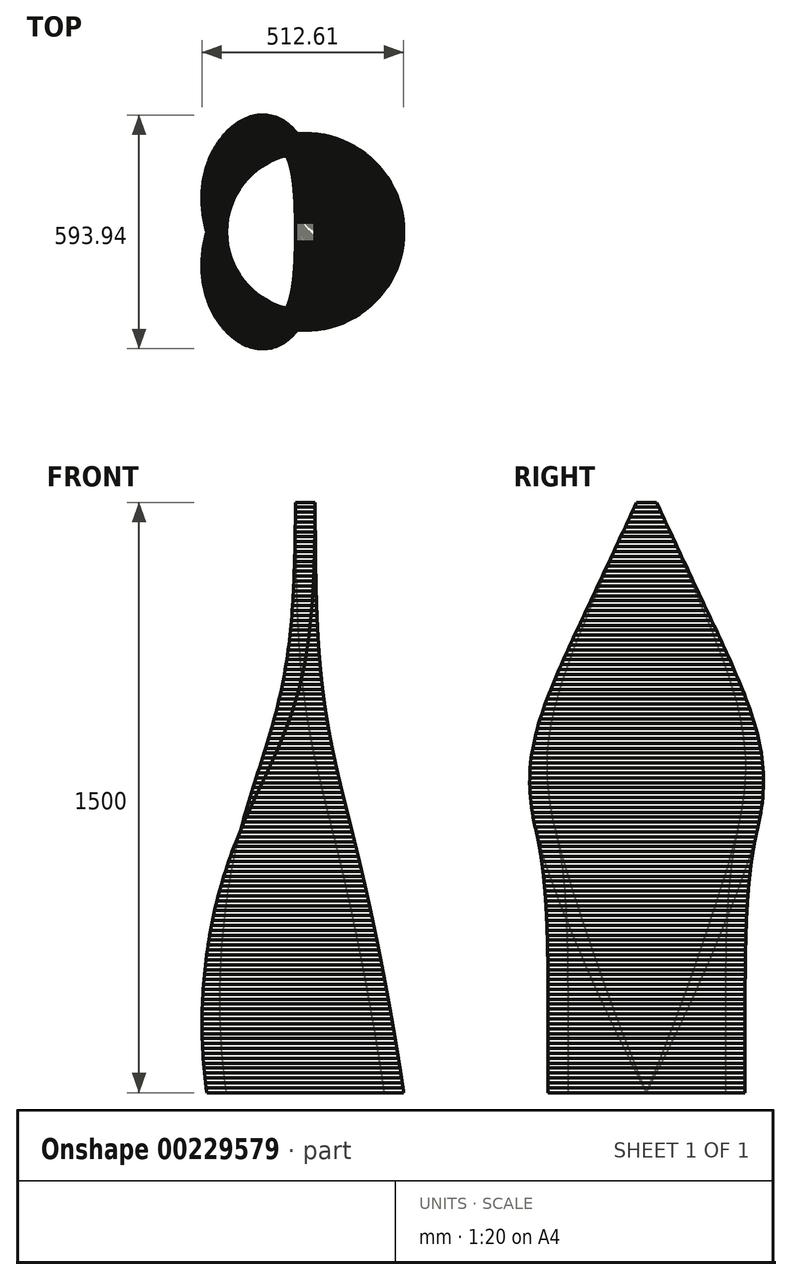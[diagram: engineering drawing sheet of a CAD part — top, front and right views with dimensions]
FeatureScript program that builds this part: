
annotation { "Feature Type Name" : "Feature", "Feature Type Description" : "" }
export const myFeature = defineFeature(function(context is Context, id is Id, definition is map)
    precondition{}
    {
        {
            var Q0;
            Q0=qCreatedBy(makeId("Top.planeOp"),FACE);
            var sketch = newSketch(context, id + "F0", { "sketchPlane" : qUnion([Q0])});
            skLineSegment(sketch, "E0", {"start": v(-200.02, 0.04) * mm, "end": v(-250.02, 0.06) * mm});
            skLineSegment(sketch, "E1", {"start": v(-200.02, -0.04) * mm, "end": v(-250.02, -0.06) * mm});
            skArc(sketch, "E2", {"start": v(-200.02, -0.04) * mm, "mid": v(199.98, 0) * mm, "end": v(-200.02, 0.04) * mm});
            skArc(sketch, "E3", {"start": v(-250.02, -0.06) * mm, "mid": v(249.98, 0) * mm, "end": v(-250.02, 0.06) * mm});
            skSolve(sketch);
        }
        {
            var Q0;
            Q0=qCreatedBy(makeId("Top.planeOp"),FACE);
            cPlane(context, id + "F1", {"entities" : qUnion([Q0]), "cplaneType" : CPlaneType.OFFSET, "offset" : 12.5 * mm, "width" : 150 * mm, "height" : 150 * mm});
        }
        {
            var Q0;
            Q0=qCreatedBy(id+"F1.planeOp",FACE);
            var sketch = newSketch(context, id + "F2", { "sketchPlane" : qUnion([Q0])});
            skLineSegment(sketch, "E4", {"start": v(-201.78, 5.1) * mm, "end": v(-251.77, 6.37) * mm});
            skLineSegment(sketch, "E5", {"start": v(-201.78, -5.1) * mm, "end": v(-251.77, -6.37) * mm});
            skArc(sketch, "E6", {"start": v(-201.78, -5.1) * mm, "mid": v(198.15, 0) * mm, "end": v(-201.78, 5.1) * mm});
            skArc(sketch, "E7", {"start": v(-251.77, -6.37) * mm, "mid": v(248.15, 0) * mm, "end": v(-251.77, 6.37) * mm});
            skSolve(sketch);
        }
        {
            var Q0;
            Q0 = qSketchRegion(id + "F0", true);
            var Q1;
            Q1 = qSketchRegion(id + "F2", true);
            loft(context, id + "F3", {"sheetProfilesArray" : [{ "sheetProfileEntities" : qUnion([Q0]) }, { "sheetProfileEntities" : qUnion([Q1]) }]});
        }
        {
            var Q0;
            Q0=qCreatedBy(makeId("Top.planeOp"),FACE);
            cPlane(context, id + "F4", {"entities" : qUnion([Q0]), "cplaneType" : CPlaneType.OFFSET, "offset" : 25 * mm, "width" : 150 * mm, "height" : 150 * mm});
        }
        {
            var Q0;
            Q0=qCreatedBy(id+"F4.planeOp",FACE);
            var sketch = newSketch(context, id + "F5", { "sketchPlane" : qUnion([Q0])});
            skLineSegment(sketch, "E8", {"start": v(-203.45, 10.14) * mm, "end": v(-253.38, 12.68) * mm});
            skLineSegment(sketch, "E9", {"start": v(-203.45, -10.14) * mm, "end": v(-253.38, -12.68) * mm});
            skArc(sketch, "E10", {"start": v(-203.45, -10.14) * mm, "mid": v(196.3, 0) * mm, "end": v(-203.45, 10.14) * mm});
            skArc(sketch, "E11", {"start": v(-253.38, -12.68) * mm, "mid": v(246.3, 0) * mm, "end": v(-253.38, 12.68) * mm});
            skSolve(sketch);
        }
        {
            var Q1;
            Q1 = qSketchRegion(id + "F2", true);
            var Q2;
            Q2 = qSketchRegion(id + "F5", true);
            loft(context, id + "F6", {"sheetProfilesArray" : [{ "sheetProfileEntities" : qUnion([Q1]) }, { "sheetProfileEntities" : qUnion([Q2]) }]});
        }
        {
            var Q0;
            Q0=qCreatedBy(id+"F1.planeOp",FACE);
            cPlane(context, id + "F7", {"entities" : qUnion([Q0]), "cplaneType" : CPlaneType.OFFSET, "offset" : 25 * mm, "width" : 150 * mm, "height" : 150 * mm});
        }
        {
            var Q0;
            Q0=qCreatedBy(id+"F7.planeOp",FACE);
            var sketch = newSketch(context, id + "F8", { "sketchPlane" : qUnion([Q0])});
            skLineSegment(sketch, "E12", {"start": v(-205.02, 15.18) * mm, "end": v(-254.87, 18.98) * mm});
            skLineSegment(sketch, "E13", {"start": v(-205.02, -15.18) * mm, "end": v(-254.87, -18.98) * mm});
            skArc(sketch, "E14", {"start": v(-205.02, -15.18) * mm, "mid": v(194.4, 0) * mm, "end": v(-205.02, 15.18) * mm});
            skArc(sketch, "E15", {"start": v(-254.87, -18.98) * mm, "mid": v(244.4, 0) * mm, "end": v(-254.87, 18.98) * mm});
            skSolve(sketch);
        }
        {
            var Q1;
            Q1 = qSketchRegion(id + "F5", true);
            var Q2;
            Q2 = qSketchRegion(id + "F8", true);
            loft(context, id + "F9", {"sheetProfilesArray" : [{ "sheetProfileEntities" : qUnion([Q1]) }, { "sheetProfileEntities" : qUnion([Q2]) }]});
        }
        {
            var Q0;
            Q0=qCreatedBy(id+"F4.planeOp",FACE);
            cPlane(context, id + "F10", {"entities" : qUnion([Q0]), "cplaneType" : CPlaneType.OFFSET, "offset" : 25 * mm, "width" : 150 * mm, "height" : 150 * mm});
        }
        {
            var Q0;
            Q0=qCreatedBy(id+"F10.planeOp",FACE);
            var sketch = newSketch(context, id + "F11", { "sketchPlane" : qUnion([Q0])});
            skLineSegment(sketch, "E16", {"start": v(-206.49, 20.21) * mm, "end": v(-256.23, 25.26) * mm});
            skLineSegment(sketch, "E17", {"start": v(-206.49, -20.21) * mm, "end": v(-256.23, -25.26) * mm});
            skArc(sketch, "E18", {"start": v(-206.49, -20.21) * mm, "mid": v(192.5, 0) * mm, "end": v(-206.49, 20.21) * mm});
            skArc(sketch, "E19", {"start": v(-256.23, -25.26) * mm, "mid": v(242.5, 0) * mm, "end": v(-256.23, 25.26) * mm});
            skSolve(sketch);
        }
        {
            var Q1;
            Q1 = qSketchRegion(id + "F8", true);
            var Q2;
            Q2 = qSketchRegion(id + "F11", true);
            loft(context, id + "F12", {"sheetProfilesArray" : [{ "sheetProfileEntities" : qUnion([Q1]) }, { "sheetProfileEntities" : qUnion([Q2]) }]});
        }
        {
            var Q0;
            Q0=qCreatedBy(id+"F7.planeOp",FACE);
            cPlane(context, id + "F13", {"entities" : qUnion([Q0]), "cplaneType" : CPlaneType.OFFSET, "offset" : 25 * mm, "width" : 150 * mm, "height" : 150 * mm});
        }
        {
            var Q0;
            Q0=qCreatedBy(id+"F13.planeOp",FACE);
            var sketch = newSketch(context, id + "F14", { "sketchPlane" : qUnion([Q0])});
            skLineSegment(sketch, "E20", {"start": v(-207.86, 25.23) * mm, "end": v(-257.46, 31.54) * mm});
            skLineSegment(sketch, "E21", {"start": v(-207.86, -25.23) * mm, "end": v(-257.46, -31.54) * mm});
            skArc(sketch, "E22", {"start": v(-207.86, -25.23) * mm, "mid": v(190.55, 0) * mm, "end": v(-207.86, 25.23) * mm});
            skArc(sketch, "E23", {"start": v(-257.46, -31.54) * mm, "mid": v(240.55, 0) * mm, "end": v(-257.46, 31.54) * mm});
            skSolve(sketch);
        }
        {
            var Q1;
            Q1 = qSketchRegion(id + "F11", true);
            var Q2;
            Q2 = qSketchRegion(id + "F14", true);
            loft(context, id + "F15", {"sheetProfilesArray" : [{ "sheetProfileEntities" : qUnion([Q1]) }, { "sheetProfileEntities" : qUnion([Q2]) }]});
        }
        {
            var Q0;
            Q0=qCreatedBy(id+"F10.planeOp",FACE);
            cPlane(context, id + "F16", {"entities" : qUnion([Q0]), "cplaneType" : CPlaneType.OFFSET, "offset" : 25 * mm, "width" : 150 * mm, "height" : 150 * mm});
        }
        {
            var Q0;
            Q0=qCreatedBy(id+"F16.planeOp",FACE);
            var sketch = newSketch(context, id + "F17", { "sketchPlane" : qUnion([Q0])});
            skLineSegment(sketch, "E24", {"start": v(-209.12, 30.23) * mm, "end": v(-258.55, 37.8) * mm});
            skLineSegment(sketch, "E25", {"start": v(-209.12, -30.23) * mm, "end": v(-258.55, -37.8) * mm});
            skArc(sketch, "E26", {"start": v(-209.12, -30.23) * mm, "mid": v(188.58, 0) * mm, "end": v(-209.12, 30.23) * mm});
            skArc(sketch, "E27", {"start": v(-258.55, -37.8) * mm, "mid": v(238.58, 0) * mm, "end": v(-258.55, 37.8) * mm});
            skSolve(sketch);
        }
        {
            var Q1;
            Q1 = qSketchRegion(id + "F14", true);
            var Q2;
            Q2 = qSketchRegion(id + "F17", true);
            loft(context, id + "F18", {"sheetProfilesArray" : [{ "sheetProfileEntities" : qUnion([Q1]) }, { "sheetProfileEntities" : qUnion([Q2]) }]});
        }
        {
            var Q0;
            Q0=qCreatedBy(id+"F13.planeOp",FACE);
            cPlane(context, id + "F19", {"entities" : qUnion([Q0]), "cplaneType" : CPlaneType.OFFSET, "offset" : 25 * mm, "width" : 150 * mm, "height" : 150 * mm});
        }
        {
            var Q0;
            Q0=qCreatedBy(id+"F19.planeOp",FACE);
            var sketch = newSketch(context, id + "F20", { "sketchPlane" : qUnion([Q0])});
            skLineSegment(sketch, "E28", {"start": v(-210.3, 35.22) * mm, "end": v(-259.51, 44.02) * mm});
            skLineSegment(sketch, "E29", {"start": v(-210.3, -35.22) * mm, "end": v(-259.51, -44.02) * mm});
            skArc(sketch, "E30", {"start": v(-210.3, -35.22) * mm, "mid": v(186.58, 0) * mm, "end": v(-210.3, 35.22) * mm});
            skArc(sketch, "E31", {"start": v(-259.51, -44.02) * mm, "mid": v(236.58, 0) * mm, "end": v(-259.51, 44.02) * mm});
            skSolve(sketch);
        }
        {
            var Q1;
            Q1 = qSketchRegion(id + "F17", true);
            var Q2;
            Q2 = qSketchRegion(id + "F20", true);
            loft(context, id + "F21", {"sheetProfilesArray" : [{ "sheetProfileEntities" : qUnion([Q1]) }, { "sheetProfileEntities" : qUnion([Q2]) }]});
        }
        {
            var Q0;
            Q0=qCreatedBy(id+"F16.planeOp",FACE);
            cPlane(context, id + "F22", {"entities" : qUnion([Q0]), "cplaneType" : CPlaneType.OFFSET, "offset" : 25 * mm, "width" : 150 * mm, "height" : 150 * mm});
        }
        {
            var Q0;
            Q0=qCreatedBy(id+"F22.planeOp",FACE);
            var sketch = newSketch(context, id + "F23", { "sketchPlane" : qUnion([Q0])});
            skLineSegment(sketch, "E32", {"start": v(-211.37, 40.18) * mm, "end": v(-260.35, 50.22) * mm});
            skLineSegment(sketch, "E33", {"start": v(-211.37, -40.18) * mm, "end": v(-260.35, -50.22) * mm});
            skArc(sketch, "E34", {"start": v(-211.37, -40.18) * mm, "mid": v(184.56, 0) * mm, "end": v(-211.37, 40.18) * mm});
            skArc(sketch, "E35", {"start": v(-260.35, -50.22) * mm, "mid": v(234.56, 0) * mm, "end": v(-260.35, 50.22) * mm});
            skSolve(sketch);
        }
        {
            var Q1;
            Q1 = qSketchRegion(id + "F20", true);
            var Q2;
            Q2 = qSketchRegion(id + "F23", true);
            loft(context, id + "F24", {"sheetProfilesArray" : [{ "sheetProfileEntities" : qUnion([Q1]) }, { "sheetProfileEntities" : qUnion([Q2]) }]});
        }
        {
            var Q0;
            Q0=qCreatedBy(id+"F19.planeOp",FACE);
            cPlane(context, id + "F25", {"entities" : qUnion([Q0]), "cplaneType" : CPlaneType.OFFSET, "offset" : 25 * mm, "width" : 150 * mm, "height" : 150 * mm});
        }
        {
            var Q0;
            Q0=qCreatedBy(id+"F25.planeOp",FACE);
            var sketch = newSketch(context, id + "F26", { "sketchPlane" : qUnion([Q0])});
            skLineSegment(sketch, "E36", {"start": v(-212.34, 45.12) * mm, "end": v(-261.05, 56.4) * mm});
            skLineSegment(sketch, "E37", {"start": v(-212.34, -45.12) * mm, "end": v(-261.05, -56.4) * mm});
            skArc(sketch, "E38", {"start": v(-212.34, -45.12) * mm, "mid": v(182.51, 0) * mm, "end": v(-212.34, 45.12) * mm});
            skArc(sketch, "E39", {"start": v(-261.05, -56.4) * mm, "mid": v(232.51, 0) * mm, "end": v(-261.05, 56.4) * mm});
            skSolve(sketch);
        }
        {
            var Q1;
            Q1 = qSketchRegion(id + "F23", true);
            var Q2;
            Q2 = qSketchRegion(id + "F26", true);
            loft(context, id + "F27", {"sheetProfilesArray" : [{ "sheetProfileEntities" : qUnion([Q1]) }, { "sheetProfileEntities" : qUnion([Q2]) }]});
        }
        {
            var Q0;
            Q0=qCreatedBy(id+"F22.planeOp",FACE);
            cPlane(context, id + "F28", {"entities" : qUnion([Q0]), "cplaneType" : CPlaneType.OFFSET, "offset" : 25 * mm, "width" : 150 * mm, "height" : 150 * mm});
        }
        {
            var Q0;
            Q0=qCreatedBy(id+"F28.planeOp",FACE);
            var sketch = newSketch(context, id + "F29", { "sketchPlane" : qUnion([Q0])});
            skLineSegment(sketch, "E40", {"start": v(-213.21, 50.03) * mm, "end": v(-261.62, 62.54) * mm});
            skLineSegment(sketch, "E41", {"start": v(-213.21, -50.03) * mm, "end": v(-261.62, -62.54) * mm});
            skArc(sketch, "E42", {"start": v(-213.21, -50.03) * mm, "mid": v(180.44, 0) * mm, "end": v(-213.21, 50.03) * mm});
            skArc(sketch, "E43", {"start": v(-261.62, -62.54) * mm, "mid": v(230.44, 0) * mm, "end": v(-261.62, 62.54) * mm});
            skSolve(sketch);
        }
        {
            var Q1;
            Q1 = qSketchRegion(id + "F26", true);
            var Q2;
            Q2 = qSketchRegion(id + "F29", true);
            loft(context, id + "F30", {"sheetProfilesArray" : [{ "sheetProfileEntities" : qUnion([Q1]) }, { "sheetProfileEntities" : qUnion([Q2]) }]});
        }
        {
            var Q0;
            Q0=qCreatedBy(id+"F25.planeOp",FACE);
            cPlane(context, id + "F31", {"entities" : qUnion([Q0]), "cplaneType" : CPlaneType.OFFSET, "offset" : 25 * mm, "width" : 150 * mm, "height" : 150 * mm});
        }
        {
            var Q0;
            Q0=qCreatedBy(id+"F31.planeOp",FACE);
            var sketch = newSketch(context, id + "F32", { "sketchPlane" : qUnion([Q0])});
            skLineSegment(sketch, "E44", {"start": v(-213.99, 54.92) * mm, "end": v(-262.07, 68.65) * mm});
            skLineSegment(sketch, "E45", {"start": v(-213.99, -54.92) * mm, "end": v(-262.07, -68.65) * mm});
            skArc(sketch, "E46", {"start": v(-213.99, -54.92) * mm, "mid": v(178.35, 0) * mm, "end": v(-213.99, 54.92) * mm});
            skArc(sketch, "E47", {"start": v(-262.07, -68.65) * mm, "mid": v(228.35, 0) * mm, "end": v(-262.07, 68.65) * mm});
            skSolve(sketch);
        }
        {
            var Q1;
            Q1 = qSketchRegion(id + "F29", true);
            var Q2;
            Q2 = qSketchRegion(id + "F32", true);
            loft(context, id + "F33", {"sheetProfilesArray" : [{ "sheetProfileEntities" : qUnion([Q1]) }, { "sheetProfileEntities" : qUnion([Q2]) }]});
        }
        {
            var Q0;
            Q0=qCreatedBy(id+"F28.planeOp",FACE);
            cPlane(context, id + "F34", {"entities" : qUnion([Q0]), "cplaneType" : CPlaneType.OFFSET, "offset" : 25 * mm, "width" : 150 * mm, "height" : 150 * mm});
        }
        {
            var Q0;
            Q0=qCreatedBy(id+"F34.planeOp",FACE);
            var sketch = newSketch(context, id + "F35", { "sketchPlane" : qUnion([Q0])});
            skLineSegment(sketch, "E48", {"start": v(-214.67, 59.77) * mm, "end": v(-262.38, 74.71) * mm});
            skLineSegment(sketch, "E49", {"start": v(-214.67, -59.77) * mm, "end": v(-262.38, -74.71) * mm});
            skArc(sketch, "E50", {"start": v(-214.67, -59.77) * mm, "mid": v(176.23, 0) * mm, "end": v(-214.67, 59.77) * mm});
            skArc(sketch, "E51", {"start": v(-262.38, -74.71) * mm, "mid": v(226.23, 0) * mm, "end": v(-262.38, 74.71) * mm});
            skSolve(sketch);
        }
        {
            var Q1;
            Q1 = qSketchRegion(id + "F32", true);
            var Q2;
            Q2 = qSketchRegion(id + "F35", true);
            loft(context, id + "F36", {"sheetProfilesArray" : [{ "sheetProfileEntities" : qUnion([Q1]) }, { "sheetProfileEntities" : qUnion([Q2]) }]});
        }
        {
            var Q0;
            Q0=qCreatedBy(id+"F31.planeOp",FACE);
            cPlane(context, id + "F37", {"entities" : qUnion([Q0]), "cplaneType" : CPlaneType.OFFSET, "offset" : 25 * mm, "width" : 150 * mm, "height" : 150 * mm});
        }
        {
            var Q0;
            Q0=qCreatedBy(id+"F37.planeOp",FACE);
            var sketch = newSketch(context, id + "F38", { "sketchPlane" : qUnion([Q0])});
            skLineSegment(sketch, "E52", {"start": v(-215.25, 64.6) * mm, "end": v(-262.57, 80.74) * mm});
            skLineSegment(sketch, "E53", {"start": v(-215.25, -64.6) * mm, "end": v(-262.57, -80.74) * mm});
            skArc(sketch, "E54", {"start": v(-215.25, -64.6) * mm, "mid": v(174.08, 0) * mm, "end": v(-215.25, 64.6) * mm});
            skArc(sketch, "E55", {"start": v(-262.57, -80.74) * mm, "mid": v(224.08, 0) * mm, "end": v(-262.57, 80.74) * mm});
            skSolve(sketch);
        }
        {
            var Q1;
            Q1 = qSketchRegion(id + "F35", true);
            var Q2;
            Q2 = qSketchRegion(id + "F38", true);
            loft(context, id + "F39", {"sheetProfilesArray" : [{ "sheetProfileEntities" : qUnion([Q1]) }, { "sheetProfileEntities" : qUnion([Q2]) }]});
        }
        {
            var Q0;
            Q0=qCreatedBy(id+"F34.planeOp",FACE);
            cPlane(context, id + "F40", {"entities" : qUnion([Q0]), "cplaneType" : CPlaneType.OFFSET, "offset" : 25 * mm, "width" : 150 * mm, "height" : 150 * mm});
        }
        {
            var Q0;
            Q0=qCreatedBy(id+"F40.planeOp",FACE);
            var sketch = newSketch(context, id + "F41", { "sketchPlane" : qUnion([Q0])});
            skLineSegment(sketch, "E56", {"start": v(-215.74, 69.39) * mm, "end": v(-262.63, 86.73) * mm});
            skLineSegment(sketch, "E57", {"start": v(-215.74, -69.39) * mm, "end": v(-262.63, -86.73) * mm});
            skArc(sketch, "E58", {"start": v(-215.74, -69.39) * mm, "mid": v(171.92, 0) * mm, "end": v(-215.74, 69.39) * mm});
            skArc(sketch, "E59", {"start": v(-262.63, -86.73) * mm, "mid": v(221.92, 0) * mm, "end": v(-262.63, 86.73) * mm});
            skSolve(sketch);
        }
        {
            var Q1;
            Q1 = qSketchRegion(id + "F38", true);
            var Q2;
            Q2 = qSketchRegion(id + "F41", true);
            loft(context, id + "F42", {"sheetProfilesArray" : [{ "sheetProfileEntities" : qUnion([Q1]) }, { "sheetProfileEntities" : qUnion([Q2]) }]});
        }
        {
            var Q0;
            Q0=qCreatedBy(id+"F37.planeOp",FACE);
            cPlane(context, id + "F43", {"entities" : qUnion([Q0]), "cplaneType" : CPlaneType.OFFSET, "offset" : 25 * mm, "width" : 150 * mm, "height" : 150 * mm});
        }
        {
            var Q0;
            Q0=qCreatedBy(id+"F43.planeOp",FACE);
            var sketch = newSketch(context, id + "F44", { "sketchPlane" : qUnion([Q0])});
            skLineSegment(sketch, "E60", {"start": v(-216.13, 74.14) * mm, "end": v(-262.57, 92.68) * mm});
            skLineSegment(sketch, "E61", {"start": v(-216.13, -74.14) * mm, "end": v(-262.57, -92.68) * mm});
            skArc(sketch, "E62", {"start": v(-216.13, -74.14) * mm, "mid": v(169.73, 0) * mm, "end": v(-216.13, 74.14) * mm});
            skArc(sketch, "E63", {"start": v(-262.57, -92.68) * mm, "mid": v(219.73, 0) * mm, "end": v(-262.57, 92.68) * mm});
            skSolve(sketch);
        }
        {
            var Q1;
            Q1 = qSketchRegion(id + "F41", true);
            var Q2;
            Q2 = qSketchRegion(id + "F44", true);
            loft(context, id + "F45", {"sheetProfilesArray" : [{ "sheetProfileEntities" : qUnion([Q1]) }, { "sheetProfileEntities" : qUnion([Q2]) }]});
        }
        {
            var Q0;
            Q0=qCreatedBy(id+"F40.planeOp",FACE);
            cPlane(context, id + "F46", {"entities" : qUnion([Q0]), "cplaneType" : CPlaneType.OFFSET, "offset" : 25 * mm, "width" : 150 * mm, "height" : 150 * mm});
        }
        {
            var Q0;
            Q0=qCreatedBy(id+"F46.planeOp",FACE);
            var sketch = newSketch(context, id + "F47", { "sketchPlane" : qUnion([Q0])});
            skLineSegment(sketch, "E64", {"start": v(-216.43, 78.87) * mm, "end": v(-262.38, 98.58) * mm});
            skLineSegment(sketch, "E65", {"start": v(-216.43, -78.87) * mm, "end": v(-262.38, -98.58) * mm});
            skArc(sketch, "E66", {"start": v(-216.43, -78.87) * mm, "mid": v(167.52, 0) * mm, "end": v(-216.43, 78.87) * mm});
            skArc(sketch, "E67", {"start": v(-262.38, -98.58) * mm, "mid": v(217.52, 0) * mm, "end": v(-262.38, 98.58) * mm});
            skSolve(sketch);
        }
        {
            var Q1;
            Q1 = qSketchRegion(id + "F44", true);
            var Q2;
            Q2 = qSketchRegion(id + "F47", true);
            loft(context, id + "F48", {"sheetProfilesArray" : [{ "sheetProfileEntities" : qUnion([Q1]) }, { "sheetProfileEntities" : qUnion([Q2]) }]});
        }
        {
            var Q0;
            Q0=qCreatedBy(id+"F43.planeOp",FACE);
            cPlane(context, id + "F49", {"entities" : qUnion([Q0]), "cplaneType" : CPlaneType.OFFSET, "offset" : 25 * mm, "width" : 150 * mm, "height" : 150 * mm});
        }
        {
            var Q0;
            Q0=qCreatedBy(id+"F49.planeOp",FACE);
            var sketch = newSketch(context, id + "F50", { "sketchPlane" : qUnion([Q0])});
            skLineSegment(sketch, "E68", {"start": v(-216.64, 83.55) * mm, "end": v(-262.07, 104.43) * mm});
            skLineSegment(sketch, "E69", {"start": v(-216.64, -83.55) * mm, "end": v(-262.07, -104.43) * mm});
            skArc(sketch, "E70", {"start": v(-216.64, -83.55) * mm, "mid": v(165.29, 0) * mm, "end": v(-216.64, 83.55) * mm});
            skArc(sketch, "E71", {"start": v(-262.07, -104.43) * mm, "mid": v(215.29, 0) * mm, "end": v(-262.07, 104.43) * mm});
            skSolve(sketch);
        }
        {
            var Q1;
            Q1 = qSketchRegion(id + "F47", true);
            var Q2;
            Q2 = qSketchRegion(id + "F50", true);
            loft(context, id + "F51", {"sheetProfilesArray" : [{ "sheetProfileEntities" : qUnion([Q1]) }, { "sheetProfileEntities" : qUnion([Q2]) }]});
        }
        {
            var Q0;
            Q0=qCreatedBy(id+"F46.planeOp",FACE);
            cPlane(context, id + "F52", {"entities" : qUnion([Q0]), "cplaneType" : CPlaneType.OFFSET, "offset" : 25 * mm, "width" : 150 * mm, "height" : 150 * mm});
        }
        {
            var Q0;
            Q0=qCreatedBy(id+"F52.planeOp",FACE);
            var sketch = newSketch(context, id + "F53", { "sketchPlane" : qUnion([Q0])});
            skLineSegment(sketch, "E72", {"start": v(-216.76, 88.2) * mm, "end": v(-261.64, 110.24) * mm});
            skLineSegment(sketch, "E73", {"start": v(-216.76, -88.2) * mm, "end": v(-261.64, -110.24) * mm});
            skArc(sketch, "E74", {"start": v(-216.76, -88.2) * mm, "mid": v(163.03, 0) * mm, "end": v(-216.76, 88.2) * mm});
            skArc(sketch, "E75", {"start": v(-261.64, -110.24) * mm, "mid": v(213.03, 0) * mm, "end": v(-261.64, 110.24) * mm});
            skSolve(sketch);
        }
        {
            var Q1;
            Q1 = qSketchRegion(id + "F50", true);
            var Q2;
            Q2 = qSketchRegion(id + "F53", true);
            loft(context, id + "F54", {"sheetProfilesArray" : [{ "sheetProfileEntities" : qUnion([Q1]) }, { "sheetProfileEntities" : qUnion([Q2]) }]});
        }
        {
            var Q0;
            Q0=qCreatedBy(id+"F49.planeOp",FACE);
            cPlane(context, id + "F55", {"entities" : qUnion([Q0]), "cplaneType" : CPlaneType.OFFSET, "offset" : 25 * mm, "width" : 150 * mm, "height" : 150 * mm});
        }
        {
            var Q0;
            Q0=qCreatedBy(id+"F55.planeOp",FACE);
            var sketch = newSketch(context, id + "F56", { "sketchPlane" : qUnion([Q0])});
            skLineSegment(sketch, "E76", {"start": v(-216.78, 92.82) * mm, "end": v(-261.08, 116) * mm});
            skLineSegment(sketch, "E77", {"start": v(-216.78, -92.82) * mm, "end": v(-261.08, -116) * mm});
            skArc(sketch, "E78", {"start": v(-216.78, -92.82) * mm, "mid": v(160.76, 0) * mm, "end": v(-216.78, 92.82) * mm});
            skArc(sketch, "E79", {"start": v(-261.08, -116) * mm, "mid": v(210.76, 0) * mm, "end": v(-261.08, 116) * mm});
            skSolve(sketch);
        }
        {
            var Q1;
            Q1 = qSketchRegion(id + "F53", true);
            var Q2;
            Q2 = qSketchRegion(id + "F56", true);
            loft(context, id + "F57", {"sheetProfilesArray" : [{ "sheetProfileEntities" : qUnion([Q1]) }, { "sheetProfileEntities" : qUnion([Q2]) }]});
        }
        {
            var Q0;
            Q0=qCreatedBy(id+"F52.planeOp",FACE);
            cPlane(context, id + "F58", {"entities" : qUnion([Q0]), "cplaneType" : CPlaneType.OFFSET, "offset" : 25 * mm, "width" : 150 * mm, "height" : 150 * mm});
        }
        {
            var Q0;
            Q0=qCreatedBy(id+"F58.planeOp",FACE);
            var sketch = newSketch(context, id + "F59", { "sketchPlane" : qUnion([Q0])});
            skLineSegment(sketch, "E80", {"start": v(-216.72, 97.4) * mm, "end": v(-260.4, 121.71) * mm});
            skLineSegment(sketch, "E81", {"start": v(-216.72, -97.4) * mm, "end": v(-260.4, -121.71) * mm});
            skArc(sketch, "E82", {"start": v(-216.72, -97.4) * mm, "mid": v(158.46, 0) * mm, "end": v(-216.72, 97.4) * mm});
            skArc(sketch, "E83", {"start": v(-260.4, -121.71) * mm, "mid": v(208.46, 0) * mm, "end": v(-260.4, 121.71) * mm});
            skSolve(sketch);
        }
        {
            var Q1;
            Q1 = qSketchRegion(id + "F56", true);
            var Q2;
            Q2 = qSketchRegion(id + "F59", true);
            loft(context, id + "F60", {"sheetProfilesArray" : [{ "sheetProfileEntities" : qUnion([Q1]) }, { "sheetProfileEntities" : qUnion([Q2]) }]});
        }
        {
            var Q0;
            Q0=qCreatedBy(id+"F55.planeOp",FACE);
            cPlane(context, id + "F61", {"entities" : qUnion([Q0]), "cplaneType" : CPlaneType.OFFSET, "offset" : 25 * mm, "width" : 150 * mm, "height" : 150 * mm});
        }
        {
            var Q0;
            Q0=qCreatedBy(id+"F61.planeOp",FACE);
            var sketch = newSketch(context, id + "F62", { "sketchPlane" : qUnion([Q0])});
            skLineSegment(sketch, "E84", {"start": v(-216.57, 101.94) * mm, "end": v(-259.6, 127.38) * mm});
            skLineSegment(sketch, "E85", {"start": v(-216.57, -101.94) * mm, "end": v(-259.6, -127.38) * mm});
            skArc(sketch, "E86", {"start": v(-216.57, -101.94) * mm, "mid": v(156.14, 0) * mm, "end": v(-216.57, 101.94) * mm});
            skArc(sketch, "E87", {"start": v(-259.6, -127.38) * mm, "mid": v(206.14, 0) * mm, "end": v(-259.6, 127.38) * mm});
            skSolve(sketch);
        }
        {
            var Q1;
            Q1 = qSketchRegion(id + "F59", true);
            var Q2;
            Q2 = qSketchRegion(id + "F62", true);
            loft(context, id + "F63", {"sheetProfilesArray" : [{ "sheetProfileEntities" : qUnion([Q1]) }, { "sheetProfileEntities" : qUnion([Q2]) }]});
        }
        {
            var Q0;
            Q0=qCreatedBy(id+"F58.planeOp",FACE);
            cPlane(context, id + "F64", {"entities" : qUnion([Q0]), "cplaneType" : CPlaneType.OFFSET, "offset" : 25 * mm, "width" : 150 * mm, "height" : 150 * mm});
        }
        {
            var Q0;
            Q0=qCreatedBy(id+"F64.planeOp",FACE);
            var sketch = newSketch(context, id + "F65", { "sketchPlane" : qUnion([Q0])});
            skLineSegment(sketch, "E88", {"start": v(-216.33, 106.44) * mm, "end": v(-258.7, 133) * mm});
            skLineSegment(sketch, "E89", {"start": v(-216.33, -106.44) * mm, "end": v(-258.7, -133) * mm});
            skArc(sketch, "E90", {"start": v(-216.33, -106.44) * mm, "mid": v(153.8, 0) * mm, "end": v(-216.33, 106.44) * mm});
            skArc(sketch, "E91", {"start": v(-258.7, -133) * mm, "mid": v(203.8, 0) * mm, "end": v(-258.7, 133) * mm});
            skSolve(sketch);
        }
        {
            var Q1;
            Q1 = qSketchRegion(id + "F62", true);
            var Q2;
            Q2 = qSketchRegion(id + "F65", true);
            loft(context, id + "F66", {"sheetProfilesArray" : [{ "sheetProfileEntities" : qUnion([Q1]) }, { "sheetProfileEntities" : qUnion([Q2]) }]});
        }
        {
            var Q0;
            Q0=qCreatedBy(id+"F61.planeOp",FACE);
            cPlane(context, id + "F67", {"entities" : qUnion([Q0]), "cplaneType" : CPlaneType.OFFSET, "offset" : 25 * mm, "width" : 150 * mm, "height" : 150 * mm});
        }
        {
            var Q0;
            Q0=qCreatedBy(id+"F67.planeOp",FACE);
            var sketch = newSketch(context, id + "F68", { "sketchPlane" : qUnion([Q0])});
            skLineSegment(sketch, "E92", {"start": v(-216, 110.92) * mm, "end": v(-257.65, 138.58) * mm});
            skLineSegment(sketch, "E93", {"start": v(-216, -110.92) * mm, "end": v(-257.65, -138.58) * mm});
            skArc(sketch, "E94", {"start": v(-216, -110.92) * mm, "mid": v(151.45, 0) * mm, "end": v(-216, 110.92) * mm});
            skArc(sketch, "E95", {"start": v(-257.65, -138.58) * mm, "mid": v(201.45, 0) * mm, "end": v(-257.65, 138.58) * mm});
            skSolve(sketch);
        }
        {
            var Q1;
            Q1 = qSketchRegion(id + "F65", true);
            var Q2;
            Q2 = qSketchRegion(id + "F68", true);
            loft(context, id + "F69", {"sheetProfilesArray" : [{ "sheetProfileEntities" : qUnion([Q1]) }, { "sheetProfileEntities" : qUnion([Q2]) }]});
        }
        {
            var Q0;
            Q0=qCreatedBy(id+"F64.planeOp",FACE);
            cPlane(context, id + "F70", {"entities" : qUnion([Q0]), "cplaneType" : CPlaneType.OFFSET, "offset" : 25 * mm, "width" : 150 * mm, "height" : 150 * mm});
        }
        {
            var Q0;
            Q0=qCreatedBy(id+"F70.planeOp",FACE);
            var sketch = newSketch(context, id + "F71", { "sketchPlane" : qUnion([Q0])});
            skLineSegment(sketch, "E96", {"start": v(-215.6, 115.35) * mm, "end": v(-256.5, 144.11) * mm});
            skLineSegment(sketch, "E97", {"start": v(-215.6, -115.35) * mm, "end": v(-256.5, -144.11) * mm});
            skArc(sketch, "E98", {"start": v(-215.6, -115.35) * mm, "mid": v(149.06, 0) * mm, "end": v(-215.6, 115.35) * mm});
            skArc(sketch, "E99", {"start": v(-256.5, -144.11) * mm, "mid": v(199.06, 0) * mm, "end": v(-256.5, 144.11) * mm});
            skSolve(sketch);
        }
        {
            var Q1;
            Q1 = qSketchRegion(id + "F68", true);
            var Q2;
            Q2 = qSketchRegion(id + "F71", true);
            loft(context, id + "F72", {"sheetProfilesArray" : [{ "sheetProfileEntities" : qUnion([Q1]) }, { "sheetProfileEntities" : qUnion([Q2]) }]});
        }
        {
            var Q0;
            Q0=qCreatedBy(id+"F67.planeOp",FACE);
            cPlane(context, id + "F73", {"entities" : qUnion([Q0]), "cplaneType" : CPlaneType.OFFSET, "offset" : 25 * mm, "width" : 150 * mm, "height" : 150 * mm});
        }
        {
            var Q0;
            Q0=qCreatedBy(id+"F73.planeOp",FACE);
            var sketch = newSketch(context, id + "F74", { "sketchPlane" : qUnion([Q0])});
            skLineSegment(sketch, "E100", {"start": v(-215.1, 119.76) * mm, "end": v(-255.23, 149.6) * mm});
            skLineSegment(sketch, "E101", {"start": v(-215.1, -119.76) * mm, "end": v(-255.23, -149.6) * mm});
            skArc(sketch, "E102", {"start": v(-215.1, -119.76) * mm, "mid": v(146.66, 0) * mm, "end": v(-215.1, 119.76) * mm});
            skArc(sketch, "E103", {"start": v(-255.23, -149.6) * mm, "mid": v(196.66, 0) * mm, "end": v(-255.23, 149.6) * mm});
            skSolve(sketch);
        }
        {
            var Q1;
            Q1 = qSketchRegion(id + "F71", true);
            var Q2;
            Q2 = qSketchRegion(id + "F74", true);
            loft(context, id + "F75", {"sheetProfilesArray" : [{ "sheetProfileEntities" : qUnion([Q1]) }, { "sheetProfileEntities" : qUnion([Q2]) }]});
        }
        {
            var Q0;
            Q0=qCreatedBy(id+"F70.planeOp",FACE);
            cPlane(context, id + "F76", {"entities" : qUnion([Q0]), "cplaneType" : CPlaneType.OFFSET, "offset" : 25 * mm, "width" : 150 * mm, "height" : 150 * mm});
        }
        {
            var Q0;
            Q0=qCreatedBy(id+"F76.planeOp",FACE);
            var sketch = newSketch(context, id + "F77", { "sketchPlane" : qUnion([Q0])});
            skLineSegment(sketch, "E104", {"start": v(-214.53, 124.14) * mm, "end": v(-253.84, 155.04) * mm});
            skLineSegment(sketch, "E105", {"start": v(-214.53, -124.14) * mm, "end": v(-253.84, -155.04) * mm});
            skArc(sketch, "E106", {"start": v(-214.53, -124.14) * mm, "mid": v(144.24, 0) * mm, "end": v(-214.53, 124.14) * mm});
            skArc(sketch, "E107", {"start": v(-253.84, -155.04) * mm, "mid": v(194.24, 0) * mm, "end": v(-253.84, 155.04) * mm});
            skSolve(sketch);
        }
        {
            var Q1;
            Q1 = qSketchRegion(id + "F74", true);
            var Q2;
            Q2 = qSketchRegion(id + "F77", true);
            loft(context, id + "F78", {"sheetProfilesArray" : [{ "sheetProfileEntities" : qUnion([Q1]) }, { "sheetProfileEntities" : qUnion([Q2]) }]});
        }
        {
            var Q0;
            Q0=qCreatedBy(id+"F73.planeOp",FACE);
            cPlane(context, id + "F79", {"entities" : qUnion([Q0]), "cplaneType" : CPlaneType.OFFSET, "offset" : 25 * mm, "width" : 150 * mm, "height" : 150 * mm});
        }
        {
            var Q0;
            Q0=qCreatedBy(id+"F79.planeOp",FACE);
            var sketch = newSketch(context, id + "F80", { "sketchPlane" : qUnion([Q0])});
            skLineSegment(sketch, "E108", {"start": v(-213.87, 128.48) * mm, "end": v(-252.33, 160.44) * mm});
            skLineSegment(sketch, "E109", {"start": v(-213.87, -128.48) * mm, "end": v(-252.33, -160.44) * mm});
            skArc(sketch, "E110", {"start": v(-213.87, -128.48) * mm, "mid": v(141.8, 0) * mm, "end": v(-213.87, 128.48) * mm});
            skArc(sketch, "E111", {"start": v(-252.33, -160.44) * mm, "mid": v(191.8, 0) * mm, "end": v(-252.33, 160.44) * mm});
            skSolve(sketch);
        }
        {
            var Q1;
            Q1 = qSketchRegion(id + "F77", true);
            var Q2;
            Q2 = qSketchRegion(id + "F80", true);
            loft(context, id + "F81", {"sheetProfilesArray" : [{ "sheetProfileEntities" : qUnion([Q1]) }, { "sheetProfileEntities" : qUnion([Q2]) }]});
        }
        {
            var Q0;
            Q0=qCreatedBy(id+"F76.planeOp",FACE);
            cPlane(context, id + "F82", {"entities" : qUnion([Q0]), "cplaneType" : CPlaneType.OFFSET, "offset" : 25 * mm, "width" : 150 * mm, "height" : 150 * mm});
        }
        {
            var Q0;
            Q0=qCreatedBy(id+"F82.planeOp",FACE);
            var sketch = newSketch(context, id + "F83", { "sketchPlane" : qUnion([Q0])});
            skLineSegment(sketch, "E112", {"start": v(-213.13, 132.8) * mm, "end": v(-250.7, 165.8) * mm});
            skLineSegment(sketch, "E113", {"start": v(-213.13, -132.8) * mm, "end": v(-250.7, -165.8) * mm});
            skArc(sketch, "E114", {"start": v(-213.13, -132.8) * mm, "mid": v(139.32, 0) * mm, "end": v(-213.13, 132.8) * mm});
            skArc(sketch, "E115", {"start": v(-250.7, -165.8) * mm, "mid": v(189.32, 0) * mm, "end": v(-250.7, 165.8) * mm});
            skSolve(sketch);
        }
        {
            var Q1;
            Q1 = qSketchRegion(id + "F80", true);
            var Q2;
            Q2 = qSketchRegion(id + "F83", true);
            loft(context, id + "F84", {"sheetProfilesArray" : [{ "sheetProfileEntities" : qUnion([Q1]) }, { "sheetProfileEntities" : qUnion([Q2]) }]});
        }
        {
            var Q0;
            Q0=qCreatedBy(id+"F79.planeOp",FACE);
            cPlane(context, id + "F85", {"entities" : qUnion([Q0]), "cplaneType" : CPlaneType.OFFSET, "offset" : 25 * mm, "width" : 150 * mm, "height" : 150 * mm});
        }
        {
            var Q0;
            Q0=qCreatedBy(id+"F85.planeOp",FACE);
            var sketch = newSketch(context, id + "F86", { "sketchPlane" : qUnion([Q0])});
            skLineSegment(sketch, "E116", {"start": v(-212.3, 137.1) * mm, "end": v(-248.95, 171.11) * mm});
            skLineSegment(sketch, "E117", {"start": v(-212.3, -137.1) * mm, "end": v(-248.95, -171.11) * mm});
            skArc(sketch, "E118", {"start": v(-212.3, -137.1) * mm, "mid": v(136.83, 0) * mm, "end": v(-212.3, 137.1) * mm});
            skArc(sketch, "E119", {"start": v(-248.95, -171.11) * mm, "mid": v(186.83, 0) * mm, "end": v(-248.95, 171.11) * mm});
            skSolve(sketch);
        }
        {
            var Q1;
            Q1 = qSketchRegion(id + "F83", true);
            var Q2;
            Q2 = qSketchRegion(id + "F86", true);
            loft(context, id + "F87", {"sheetProfilesArray" : [{ "sheetProfileEntities" : qUnion([Q1]) }, { "sheetProfileEntities" : qUnion([Q2]) }]});
        }
        {
            var Q0;
            Q0=qCreatedBy(id+"F82.planeOp",FACE);
            cPlane(context, id + "F88", {"entities" : qUnion([Q0]), "cplaneType" : CPlaneType.OFFSET, "offset" : 25 * mm, "width" : 150 * mm, "height" : 150 * mm});
        }
        {
            var Q0;
            Q0=qCreatedBy(id+"F88.planeOp",FACE);
            var sketch = newSketch(context, id + "F89", { "sketchPlane" : qUnion([Q0])});
            skLineSegment(sketch, "E120", {"start": v(-211.4, 141.36) * mm, "end": v(-247.08, 176.39) * mm});
            skLineSegment(sketch, "E121", {"start": v(-211.4, -141.36) * mm, "end": v(-247.08, -176.39) * mm});
            skArc(sketch, "E122", {"start": v(-211.4, -141.36) * mm, "mid": v(134.32, 0) * mm, "end": v(-211.4, 141.36) * mm});
            skArc(sketch, "E123", {"start": v(-247.08, -176.39) * mm, "mid": v(184.32, 0) * mm, "end": v(-247.08, 176.39) * mm});
            skSolve(sketch);
        }
        {
            var Q1;
            Q1 = qSketchRegion(id + "F86", true);
            var Q2;
            Q2 = qSketchRegion(id + "F89", true);
            loft(context, id + "F90", {"sheetProfilesArray" : [{ "sheetProfileEntities" : qUnion([Q1]) }, { "sheetProfileEntities" : qUnion([Q2]) }]});
        }
        {
            var Q0;
            Q0=qCreatedBy(id+"F85.planeOp",FACE);
            cPlane(context, id + "F91", {"entities" : qUnion([Q0]), "cplaneType" : CPlaneType.OFFSET, "offset" : 25 * mm, "width" : 150 * mm, "height" : 150 * mm});
        }
        {
            var Q0;
            Q0=qCreatedBy(id+"F91.planeOp",FACE);
            var sketch = newSketch(context, id + "F92", { "sketchPlane" : qUnion([Q0])});
            skLineSegment(sketch, "E124", {"start": v(-210.41, 145.6) * mm, "end": v(-245.08, 181.62) * mm});
            skLineSegment(sketch, "E125", {"start": v(-210.41, -145.6) * mm, "end": v(-245.08, -181.62) * mm});
            skArc(sketch, "E126", {"start": v(-210.41, -145.6) * mm, "mid": v(131.78, 0) * mm, "end": v(-210.41, 145.6) * mm});
            skArc(sketch, "E127", {"start": v(-245.08, -181.62) * mm, "mid": v(181.78, 0) * mm, "end": v(-245.08, 181.62) * mm});
            skSolve(sketch);
        }
        {
            var Q1;
            Q1 = qSketchRegion(id + "F89", true);
            var Q2;
            Q2 = qSketchRegion(id + "F92", true);
            loft(context, id + "F93", {"sheetProfilesArray" : [{ "sheetProfileEntities" : qUnion([Q1]) }, { "sheetProfileEntities" : qUnion([Q2]) }]});
        }
        {
            var Q0;
            Q0=qCreatedBy(id+"F88.planeOp",FACE);
            cPlane(context, id + "F94", {"entities" : qUnion([Q0]), "cplaneType" : CPlaneType.OFFSET, "offset" : 25 * mm, "width" : 150 * mm, "height" : 150 * mm});
        }
        {
            var Q0;
            Q0=qCreatedBy(id+"F94.planeOp",FACE);
            var sketch = newSketch(context, id + "F95", { "sketchPlane" : qUnion([Q0])});
            skLineSegment(sketch, "E128", {"start": v(-209.34, 149.81) * mm, "end": v(-242.97, 186.82) * mm});
            skLineSegment(sketch, "E129", {"start": v(-209.34, -149.81) * mm, "end": v(-242.97, -186.82) * mm});
            skArc(sketch, "E130", {"start": v(-209.34, -149.81) * mm, "mid": v(129.22, 0) * mm, "end": v(-209.34, 149.81) * mm});
            skArc(sketch, "E131", {"start": v(-242.97, -186.82) * mm, "mid": v(179.22, 0) * mm, "end": v(-242.97, 186.82) * mm});
            skSolve(sketch);
        }
        {
            var Q1;
            Q1 = qSketchRegion(id + "F92", true);
            var Q2;
            Q2 = qSketchRegion(id + "F95", true);
            loft(context, id + "F96", {"sheetProfilesArray" : [{ "sheetProfileEntities" : qUnion([Q1]) }, { "sheetProfileEntities" : qUnion([Q2]) }]});
        }
        {
            var Q0;
            Q0=qCreatedBy(id+"F91.planeOp",FACE);
            cPlane(context, id + "F97", {"entities" : qUnion([Q0]), "cplaneType" : CPlaneType.OFFSET, "offset" : 25 * mm, "width" : 150 * mm, "height" : 150 * mm});
        }
        {
            var Q0;
            Q0=qCreatedBy(id+"F97.planeOp",FACE);
            var sketch = newSketch(context, id + "F98", { "sketchPlane" : qUnion([Q0])});
            skLineSegment(sketch, "E132", {"start": v(-208.2, 154) * mm, "end": v(-240.73, 191.97) * mm});
            skLineSegment(sketch, "E133", {"start": v(-208.2, -154) * mm, "end": v(-240.73, -191.97) * mm});
            skArc(sketch, "E134", {"start": v(-208.2, -154) * mm, "mid": v(126.63, 0) * mm, "end": v(-208.2, 154) * mm});
            skArc(sketch, "E135", {"start": v(-240.73, -191.97) * mm, "mid": v(176.63, 0) * mm, "end": v(-240.73, 191.97) * mm});
            skSolve(sketch);
        }
        {
            var Q1;
            Q1 = qSketchRegion(id + "F95", true);
            var Q2;
            Q2 = qSketchRegion(id + "F98", true);
            loft(context, id + "F99", {"sheetProfilesArray" : [{ "sheetProfileEntities" : qUnion([Q1]) }, { "sheetProfileEntities" : qUnion([Q2]) }]});
        }
        {
            var Q0;
            Q0=qCreatedBy(id+"F94.planeOp",FACE);
            cPlane(context, id + "F100", {"entities" : qUnion([Q0]), "cplaneType" : CPlaneType.OFFSET, "offset" : 25 * mm, "width" : 150 * mm, "height" : 150 * mm});
        }
        {
            var Q0;
            Q0=qCreatedBy(id+"F100.planeOp",FACE);
            var sketch = newSketch(context, id + "F101", { "sketchPlane" : qUnion([Q0])});
            skLineSegment(sketch, "E136", {"start": v(-206.95, 158.18) * mm, "end": v(-238.36, 197.09) * mm});
            skLineSegment(sketch, "E137", {"start": v(-206.95, -158.18) * mm, "end": v(-238.36, -197.09) * mm});
            skArc(sketch, "E138", {"start": v(-206.95, -158.18) * mm, "mid": v(124.02, 0) * mm, "end": v(-206.95, 158.18) * mm});
            skArc(sketch, "E139", {"start": v(-238.36, -197.09) * mm, "mid": v(174.02, 0) * mm, "end": v(-238.36, 197.09) * mm});
            skSolve(sketch);
        }
        {
            var Q1;
            Q1 = qSketchRegion(id + "F98", true);
            var Q2;
            Q2 = qSketchRegion(id + "F101", true);
            loft(context, id + "F102", {"sheetProfilesArray" : [{ "sheetProfileEntities" : qUnion([Q1]) }, { "sheetProfileEntities" : qUnion([Q2]) }]});
        }
        {
            var Q0;
            Q0=qCreatedBy(id+"F97.planeOp",FACE);
            cPlane(context, id + "F103", {"entities" : qUnion([Q0]), "cplaneType" : CPlaneType.OFFSET, "offset" : 25 * mm, "width" : 150 * mm, "height" : 150 * mm});
        }
        {
            var Q0;
            Q0=qCreatedBy(id+"F103.planeOp",FACE);
            var sketch = newSketch(context, id + "F104", { "sketchPlane" : qUnion([Q0])});
            skLineSegment(sketch, "E140", {"start": v(-205.63, 162.33) * mm, "end": v(-235.86, 202.16) * mm});
            skLineSegment(sketch, "E141", {"start": v(-205.63, -162.33) * mm, "end": v(-235.86, -202.16) * mm});
            skArc(sketch, "E142", {"start": v(-205.63, -162.33) * mm, "mid": v(121.38, 0) * mm, "end": v(-205.63, 162.33) * mm});
            skArc(sketch, "E143", {"start": v(-235.86, -202.16) * mm, "mid": v(171.38, 0) * mm, "end": v(-235.86, 202.16) * mm});
            skSolve(sketch);
        }
        {
            var Q1;
            Q1 = qSketchRegion(id + "F101", true);
            var Q2;
            Q2 = qSketchRegion(id + "F104", true);
            loft(context, id + "F105", {"sheetProfilesArray" : [{ "sheetProfileEntities" : qUnion([Q1]) }, { "sheetProfileEntities" : qUnion([Q2]) }]});
        }
        {
            var Q0;
            Q0=qCreatedBy(id+"F100.planeOp",FACE);
            cPlane(context, id + "F106", {"entities" : qUnion([Q0]), "cplaneType" : CPlaneType.OFFSET, "offset" : 25 * mm, "width" : 150 * mm, "height" : 150 * mm});
        }
        {
            var Q0;
            Q0=qCreatedBy(id+"F106.planeOp",FACE);
            var sketch = newSketch(context, id + "F107", { "sketchPlane" : qUnion([Q0])});
            skLineSegment(sketch, "E144", {"start": v(-204.23, 166.46) * mm, "end": v(-233.24, 207.19) * mm});
            skLineSegment(sketch, "E145", {"start": v(-204.23, -166.46) * mm, "end": v(-233.24, -207.19) * mm});
            skArc(sketch, "E146", {"start": v(-204.23, -166.46) * mm, "mid": v(118.72, 0) * mm, "end": v(-204.23, 166.46) * mm});
            skArc(sketch, "E147", {"start": v(-233.24, -207.19) * mm, "mid": v(168.72, 0) * mm, "end": v(-233.24, 207.19) * mm});
            skSolve(sketch);
        }
        {
            var Q1;
            Q1 = qSketchRegion(id + "F104", true);
            var Q2;
            Q2 = qSketchRegion(id + "F107", true);
            loft(context, id + "F108", {"sheetProfilesArray" : [{ "sheetProfileEntities" : qUnion([Q1]) }, { "sheetProfileEntities" : qUnion([Q2]) }]});
        }
        {
            var Q0;
            Q0=qCreatedBy(id+"F103.planeOp",FACE);
            cPlane(context, id + "F109", {"entities" : qUnion([Q0]), "cplaneType" : CPlaneType.OFFSET, "offset" : 25 * mm, "width" : 150 * mm, "height" : 150 * mm});
        }
        {
            var Q0;
            Q0=qCreatedBy(id+"F109.planeOp",FACE);
            var sketch = newSketch(context, id + "F110", { "sketchPlane" : qUnion([Q0])});
            skLineSegment(sketch, "E148", {"start": v(-202.73, 170.57) * mm, "end": v(-230.47, 212.17) * mm});
            skLineSegment(sketch, "E149", {"start": v(-202.73, -170.57) * mm, "end": v(-230.47, -212.17) * mm});
            skArc(sketch, "E150", {"start": v(-202.73, -170.57) * mm, "mid": v(116.02, 0) * mm, "end": v(-202.73, 170.57) * mm});
            skArc(sketch, "E151", {"start": v(-230.47, -212.17) * mm, "mid": v(166.02, 0) * mm, "end": v(-230.47, 212.17) * mm});
            skSolve(sketch);
        }
        {
            var Q1;
            Q1 = qSketchRegion(id + "F107", true);
            var Q2;
            Q2 = qSketchRegion(id + "F110", true);
            loft(context, id + "F111", {"sheetProfilesArray" : [{ "sheetProfileEntities" : qUnion([Q1]) }, { "sheetProfileEntities" : qUnion([Q2]) }]});
        }
        {
            var Q0;
            Q0=qCreatedBy(id+"F106.planeOp",FACE);
            cPlane(context, id + "F112", {"entities" : qUnion([Q0]), "cplaneType" : CPlaneType.OFFSET, "offset" : 25 * mm, "width" : 150 * mm, "height" : 150 * mm});
        }
        {
            var Q0;
            Q0=qCreatedBy(id+"F112.planeOp",FACE);
            var sketch = newSketch(context, id + "F113", { "sketchPlane" : qUnion([Q0])});
            skLineSegment(sketch, "E152", {"start": v(-201.15, 174.66) * mm, "end": v(-227.57, 217.1) * mm});
            skLineSegment(sketch, "E153", {"start": v(-201.15, -174.66) * mm, "end": v(-227.57, -217.1) * mm});
            skArc(sketch, "E154", {"start": v(-201.15, -174.66) * mm, "mid": v(113.3, 0) * mm, "end": v(-201.15, 174.66) * mm});
            skArc(sketch, "E155", {"start": v(-227.57, -217.1) * mm, "mid": v(163.3, 0) * mm, "end": v(-227.57, 217.1) * mm});
            skSolve(sketch);
        }
        {
            var Q1;
            Q1 = qSketchRegion(id + "F110", true);
            var Q2;
            Q2 = qSketchRegion(id + "F113", true);
            loft(context, id + "F114", {"sheetProfilesArray" : [{ "sheetProfileEntities" : qUnion([Q1]) }, { "sheetProfileEntities" : qUnion([Q2]) }]});
        }
        {
            var Q0;
            Q0=qCreatedBy(id+"F109.planeOp",FACE);
            cPlane(context, id + "F115", {"entities" : qUnion([Q0]), "cplaneType" : CPlaneType.OFFSET, "offset" : 25 * mm, "width" : 150 * mm, "height" : 150 * mm});
        }
        {
            var Q0;
            Q0=qCreatedBy(id+"F115.planeOp",FACE);
            var sketch = newSketch(context, id + "F116", { "sketchPlane" : qUnion([Q0])});
            skLineSegment(sketch, "E156", {"start": v(-199.48, 178.72) * mm, "end": v(-224.53, 221.99) * mm});
            skLineSegment(sketch, "E157", {"start": v(-199.48, -178.72) * mm, "end": v(-224.53, -221.99) * mm});
            skArc(sketch, "E158", {"start": v(-199.48, -178.72) * mm, "mid": v(110.56, 0) * mm, "end": v(-199.48, 178.72) * mm});
            skArc(sketch, "E159", {"start": v(-224.53, -221.99) * mm, "mid": v(160.56, 0) * mm, "end": v(-224.53, 221.99) * mm});
            skSolve(sketch);
        }
        {
            var Q1;
            Q1 = qSketchRegion(id + "F113", true);
            var Q2;
            Q2 = qSketchRegion(id + "F116", true);
            loft(context, id + "F117", {"sheetProfilesArray" : [{ "sheetProfileEntities" : qUnion([Q1]) }, { "sheetProfileEntities" : qUnion([Q2]) }]});
        }
        {
            var Q0;
            Q0=qCreatedBy(id+"F112.planeOp",FACE);
            cPlane(context, id + "F118", {"entities" : qUnion([Q0]), "cplaneType" : CPlaneType.OFFSET, "offset" : 25 * mm, "width" : 150 * mm, "height" : 150 * mm});
        }
        {
            var Q0;
            Q0=qCreatedBy(id+"F118.planeOp",FACE);
            var sketch = newSketch(context, id + "F119", { "sketchPlane" : qUnion([Q0])});
            skLineSegment(sketch, "E160", {"start": v(-197.7, 182.75) * mm, "end": v(-221.35, 226.8) * mm});
            skLineSegment(sketch, "E161", {"start": v(-197.7, -182.75) * mm, "end": v(-221.35, -226.8) * mm});
            skArc(sketch, "E162", {"start": v(-197.7, -182.75) * mm, "mid": v(107.78, 0) * mm, "end": v(-197.7, 182.75) * mm});
            skArc(sketch, "E163", {"start": v(-221.35, -226.8) * mm, "mid": v(157.78, 0) * mm, "end": v(-221.35, 226.8) * mm});
            skSolve(sketch);
        }
        {
            var Q1;
            Q1 = qSketchRegion(id + "F116", true);
            var Q2;
            Q2 = qSketchRegion(id + "F119", true);
            loft(context, id + "F120", {"sheetProfilesArray" : [{ "sheetProfileEntities" : qUnion([Q1]) }, { "sheetProfileEntities" : qUnion([Q2]) }]});
        }
        {
            var Q0;
            Q0=qCreatedBy(id+"F115.planeOp",FACE);
            cPlane(context, id + "F121", {"entities" : qUnion([Q0]), "cplaneType" : CPlaneType.OFFSET, "offset" : 25 * mm, "width" : 150 * mm, "height" : 150 * mm});
        }
        {
            var Q0;
            Q0=qCreatedBy(id+"F121.planeOp",FACE);
            var sketch = newSketch(context, id + "F122", { "sketchPlane" : qUnion([Q0])});
            skLineSegment(sketch, "E164", {"start": v(-195.85, 186.76) * mm, "end": v(-218.03, 231.57) * mm});
            skLineSegment(sketch, "E165", {"start": v(-195.85, -186.76) * mm, "end": v(-218.03, -231.57) * mm});
            skArc(sketch, "E166", {"start": v(-195.85, -186.76) * mm, "mid": v(104.97, 0) * mm, "end": v(-195.85, 186.76) * mm});
            skArc(sketch, "E167", {"start": v(-218.03, -231.57) * mm, "mid": v(154.97, 0) * mm, "end": v(-218.03, 231.57) * mm});
            skSolve(sketch);
        }
        {
            var Q1;
            Q1 = qSketchRegion(id + "F119", true);
            var Q2;
            Q2 = qSketchRegion(id + "F122", true);
            loft(context, id + "F123", {"sheetProfilesArray" : [{ "sheetProfileEntities" : qUnion([Q1]) }, { "sheetProfileEntities" : qUnion([Q2]) }]});
        }
        {
            var Q0;
            Q0=qCreatedBy(id+"F118.planeOp",FACE);
            cPlane(context, id + "F124", {"entities" : qUnion([Q0]), "cplaneType" : CPlaneType.OFFSET, "offset" : 25 * mm, "width" : 150 * mm, "height" : 150 * mm});
        }
        {
            var Q0;
            Q0=qCreatedBy(id+"F124.planeOp",FACE);
            var sketch = newSketch(context, id + "F125", { "sketchPlane" : qUnion([Q0])});
            skLineSegment(sketch, "E168", {"start": v(-193.89, 190.73) * mm, "end": v(-214.55, 236.26) * mm});
            skLineSegment(sketch, "E169", {"start": v(-193.89, -190.73) * mm, "end": v(-214.55, -236.26) * mm});
            skArc(sketch, "E170", {"start": v(-193.89, -190.73) * mm, "mid": v(102.14, 0) * mm, "end": v(-193.89, 190.73) * mm});
            skArc(sketch, "E171", {"start": v(-214.55, -236.26) * mm, "mid": v(152.14, 0) * mm, "end": v(-214.55, 236.26) * mm});
            skSolve(sketch);
        }
        {
            var Q1;
            Q1 = qSketchRegion(id + "F122", true);
            var Q2;
            Q2 = qSketchRegion(id + "F125", true);
            loft(context, id + "F126", {"sheetProfilesArray" : [{ "sheetProfileEntities" : qUnion([Q1]) }, { "sheetProfileEntities" : qUnion([Q2]) }]});
        }
        {
            var Q0;
            Q0=qCreatedBy(id+"F121.planeOp",FACE);
            cPlane(context, id + "F127", {"entities" : qUnion([Q0]), "cplaneType" : CPlaneType.OFFSET, "offset" : 25 * mm, "width" : 150 * mm, "height" : 150 * mm});
        }
        {
            var Q0;
            Q0=qCreatedBy(id+"F127.planeOp",FACE);
            var sketch = newSketch(context, id + "F128", { "sketchPlane" : qUnion([Q0])});
            skLineSegment(sketch, "E172", {"start": v(-191.83, 194.66) * mm, "end": v(-210.93, 240.87) * mm});
            skLineSegment(sketch, "E173", {"start": v(-191.83, -194.66) * mm, "end": v(-210.93, -240.87) * mm});
            skArc(sketch, "E174", {"start": v(-191.83, -194.66) * mm, "mid": v(99.27, 0) * mm, "end": v(-191.83, 194.66) * mm});
            skArc(sketch, "E175", {"start": v(-210.93, -240.87) * mm, "mid": v(149.27, 0) * mm, "end": v(-210.93, 240.87) * mm});
            skSolve(sketch);
        }
        {
            var Q1;
            Q1 = qSketchRegion(id + "F125", true);
            var Q2;
            Q2 = qSketchRegion(id + "F128", true);
            loft(context, id + "F129", {"sheetProfilesArray" : [{ "sheetProfileEntities" : qUnion([Q1]) }, { "sheetProfileEntities" : qUnion([Q2]) }]});
        }
        {
            var Q0;
            Q0=qCreatedBy(id+"F124.planeOp",FACE);
            cPlane(context, id + "F130", {"entities" : qUnion([Q0]), "cplaneType" : CPlaneType.OFFSET, "offset" : 25 * mm, "width" : 150 * mm, "height" : 150 * mm});
        }
        {
            var Q0;
            Q0=qCreatedBy(id+"F130.planeOp",FACE);
            var sketch = newSketch(context, id + "F131", { "sketchPlane" : qUnion([Q0])});
            skLineSegment(sketch, "E176", {"start": v(-189.67, 198.55) * mm, "end": v(-207.15, 245.4) * mm});
            skLineSegment(sketch, "E177", {"start": v(-189.67, -198.55) * mm, "end": v(-207.15, -245.4) * mm});
            skArc(sketch, "E178", {"start": v(-189.67, -198.55) * mm, "mid": v(96.38, 0) * mm, "end": v(-189.67, 198.55) * mm});
            skArc(sketch, "E179", {"start": v(-207.15, -245.4) * mm, "mid": v(146.38, 0) * mm, "end": v(-207.15, 245.4) * mm});
            skSolve(sketch);
        }
        {
            var Q1;
            Q1 = qSketchRegion(id + "F128", true);
            var Q2;
            Q2 = qSketchRegion(id + "F131", true);
            loft(context, id + "F132", {"sheetProfilesArray" : [{ "sheetProfileEntities" : qUnion([Q1]) }, { "sheetProfileEntities" : qUnion([Q2]) }]});
        }
        {
            var Q0;
            Q0=qCreatedBy(id+"F127.planeOp",FACE);
            cPlane(context, id + "F133", {"entities" : qUnion([Q0]), "cplaneType" : CPlaneType.OFFSET, "offset" : 25 * mm, "width" : 150 * mm, "height" : 150 * mm});
        }
        {
            var Q0;
            Q0=qCreatedBy(id+"F133.planeOp",FACE);
            var sketch = newSketch(context, id + "F134", { "sketchPlane" : qUnion([Q0])});
            skLineSegment(sketch, "E180", {"start": v(-187.4, 202.39) * mm, "end": v(-203.22, 249.82) * mm});
            skLineSegment(sketch, "E181", {"start": v(-187.4, -202.39) * mm, "end": v(-203.22, -249.82) * mm});
            skArc(sketch, "E182", {"start": v(-187.4, -202.39) * mm, "mid": v(93.45, 0) * mm, "end": v(-187.4, 202.39) * mm});
            skArc(sketch, "E183", {"start": v(-203.22, -249.82) * mm, "mid": v(143.45, 0) * mm, "end": v(-203.22, 249.82) * mm});
            skSolve(sketch);
        }
        {
            var Q1;
            Q1 = qSketchRegion(id + "F131", true);
            var Q2;
            Q2 = qSketchRegion(id + "F134", true);
            loft(context, id + "F135", {"sheetProfilesArray" : [{ "sheetProfileEntities" : qUnion([Q1]) }, { "sheetProfileEntities" : qUnion([Q2]) }]});
        }
        {
            var Q0;
            Q0=qCreatedBy(id+"F130.planeOp",FACE);
            cPlane(context, id + "F136", {"entities" : qUnion([Q0]), "cplaneType" : CPlaneType.OFFSET, "offset" : 25 * mm, "width" : 150 * mm, "height" : 150 * mm});
        }
        {
            var Q0;
            Q0=qCreatedBy(id+"F136.planeOp",FACE);
            var sketch = newSketch(context, id + "F137", { "sketchPlane" : qUnion([Q0])});
            skLineSegment(sketch, "E184", {"start": v(-185.03, 206.17) * mm, "end": v(-199.14, 254.14) * mm});
            skLineSegment(sketch, "E185", {"start": v(-185.03, -206.17) * mm, "end": v(-199.14, -254.14) * mm});
            skArc(sketch, "E186", {"start": v(-185.03, -206.17) * mm, "mid": v(90.5, 0) * mm, "end": v(-185.03, 206.17) * mm});
            skArc(sketch, "E187", {"start": v(-199.14, -254.14) * mm, "mid": v(140.5, 0) * mm, "end": v(-199.14, 254.14) * mm});
            skSolve(sketch);
        }
        {
            var Q1;
            Q1 = qSketchRegion(id + "F134", true);
            var Q2;
            Q2 = qSketchRegion(id + "F137", true);
            loft(context, id + "F138", {"sheetProfilesArray" : [{ "sheetProfileEntities" : qUnion([Q1]) }, { "sheetProfileEntities" : qUnion([Q2]) }]});
        }
        {
            var Q0;
            Q0=qCreatedBy(id+"F133.planeOp",FACE);
            cPlane(context, id + "F139", {"entities" : qUnion([Q0]), "cplaneType" : CPlaneType.OFFSET, "offset" : 25 * mm, "width" : 150 * mm, "height" : 150 * mm});
        }
        {
            var Q0;
            Q0=qCreatedBy(id+"F139.planeOp",FACE);
            var sketch = newSketch(context, id + "F140", { "sketchPlane" : qUnion([Q0])});
            skLineSegment(sketch, "E188", {"start": v(-182.55, 209.88) * mm, "end": v(-194.9, 258.34) * mm});
            skLineSegment(sketch, "E189", {"start": v(-182.55, -209.88) * mm, "end": v(-194.9, -258.34) * mm});
            skArc(sketch, "E190", {"start": v(-182.55, -209.88) * mm, "mid": v(87.52, 0) * mm, "end": v(-182.55, 209.88) * mm});
            skArc(sketch, "E191", {"start": v(-194.9, -258.34) * mm, "mid": v(137.52, 0) * mm, "end": v(-194.9, 258.34) * mm});
            skSolve(sketch);
        }
        {
            var Q1;
            Q1 = qSketchRegion(id + "F137", true);
            var Q2;
            Q2 = qSketchRegion(id + "F140", true);
            loft(context, id + "F141", {"sheetProfilesArray" : [{ "sheetProfileEntities" : qUnion([Q1]) }, { "sheetProfileEntities" : qUnion([Q2]) }]});
        }
        {
            var Q0;
            Q0=qCreatedBy(id+"F136.planeOp",FACE);
            cPlane(context, id + "F142", {"entities" : qUnion([Q0]), "cplaneType" : CPlaneType.OFFSET, "offset" : 25 * mm, "width" : 150 * mm, "height" : 150 * mm});
        }
        {
            var Q0;
            Q0=qCreatedBy(id+"F142.planeOp",FACE);
            var sketch = newSketch(context, id + "F143", { "sketchPlane" : qUnion([Q0])});
            skLineSegment(sketch, "E192", {"start": v(-179.96, 213.52) * mm, "end": v(-190.5, 262.4) * mm});
            skLineSegment(sketch, "E193", {"start": v(-179.96, -213.52) * mm, "end": v(-190.5, -262.4) * mm});
            skArc(sketch, "E194", {"start": v(-179.96, -213.52) * mm, "mid": v(84.52, 0) * mm, "end": v(-179.96, 213.52) * mm});
            skArc(sketch, "E195", {"start": v(-190.5, -262.4) * mm, "mid": v(134.52, 0) * mm, "end": v(-190.5, 262.4) * mm});
            skSolve(sketch);
        }
        {
            var Q1;
            Q1 = qSketchRegion(id + "F140", true);
            var Q2;
            Q2 = qSketchRegion(id + "F143", true);
            loft(context, id + "F144", {"sheetProfilesArray" : [{ "sheetProfileEntities" : qUnion([Q1]) }, { "sheetProfileEntities" : qUnion([Q2]) }]});
        }
        {
            var Q0;
            Q0=qCreatedBy(id+"F139.planeOp",FACE);
            cPlane(context, id + "F145", {"entities" : qUnion([Q0]), "cplaneType" : CPlaneType.OFFSET, "offset" : 25 * mm, "width" : 150 * mm, "height" : 150 * mm});
        }
        {
            var Q0;
            Q0=qCreatedBy(id+"F145.planeOp",FACE);
            var sketch = newSketch(context, id + "F146", { "sketchPlane" : qUnion([Q0])});
            skLineSegment(sketch, "E196", {"start": v(-177.26, 217.08) * mm, "end": v(-185.95, 266.32) * mm});
            skLineSegment(sketch, "E197", {"start": v(-177.26, -217.08) * mm, "end": v(-185.95, -266.32) * mm});
            skArc(sketch, "E198", {"start": v(-177.26, -217.08) * mm, "mid": v(81.49, 0) * mm, "end": v(-177.26, 217.08) * mm});
            skArc(sketch, "E199", {"start": v(-185.95, -266.32) * mm, "mid": v(131.49, 0) * mm, "end": v(-185.95, 266.32) * mm});
            skSolve(sketch);
        }
        {
            var Q1;
            Q1 = qSketchRegion(id + "F143", true);
            var Q2;
            Q2 = qSketchRegion(id + "F146", true);
            loft(context, id + "F147", {"sheetProfilesArray" : [{ "sheetProfileEntities" : qUnion([Q1]) }, { "sheetProfileEntities" : qUnion([Q2]) }]});
        }
        {
            var Q0;
            Q0=qCreatedBy(id+"F142.planeOp",FACE);
            cPlane(context, id + "F148", {"entities" : qUnion([Q0]), "cplaneType" : CPlaneType.OFFSET, "offset" : 25 * mm, "width" : 150 * mm, "height" : 150 * mm});
        }
        {
            var Q0;
            Q0=qCreatedBy(id+"F148.planeOp",FACE);
            var sketch = newSketch(context, id + "F149", { "sketchPlane" : qUnion([Q0])});
            skLineSegment(sketch, "E200", {"start": v(-174.45, 220.54) * mm, "end": v(-181.25, 270.07) * mm});
            skLineSegment(sketch, "E201", {"start": v(-174.45, -220.54) * mm, "end": v(-181.25, -270.07) * mm});
            skArc(sketch, "E202", {"start": v(-174.45, -220.54) * mm, "mid": v(78.43, 0) * mm, "end": v(-174.45, 220.54) * mm});
            skArc(sketch, "E203", {"start": v(-181.25, -270.07) * mm, "mid": v(128.43, 0) * mm, "end": v(-181.25, 270.07) * mm});
            skSolve(sketch);
        }
        {
            var Q1;
            Q1 = qSketchRegion(id + "F146", true);
            var Q2;
            Q2 = qSketchRegion(id + "F149", true);
            loft(context, id + "F150", {"sheetProfilesArray" : [{ "sheetProfileEntities" : qUnion([Q1]) }, { "sheetProfileEntities" : qUnion([Q2]) }]});
        }
        {
            var Q0;
            Q0=qCreatedBy(id+"F145.planeOp",FACE);
            cPlane(context, id + "F151", {"entities" : qUnion([Q0]), "cplaneType" : CPlaneType.OFFSET, "offset" : 25 * mm, "width" : 150 * mm, "height" : 150 * mm});
        }
        {
            var Q0;
            Q0=qCreatedBy(id+"F151.planeOp",FACE);
            var sketch = newSketch(context, id + "F152", { "sketchPlane" : qUnion([Q0])});
            skLineSegment(sketch, "E204", {"start": v(-171.53, 223.89) * mm, "end": v(-176.4, 273.65) * mm});
            skLineSegment(sketch, "E205", {"start": v(-171.53, -223.89) * mm, "end": v(-176.4, -273.65) * mm});
            skArc(sketch, "E206", {"start": v(-171.53, -223.89) * mm, "mid": v(75.36, 0) * mm, "end": v(-171.53, 223.89) * mm});
            skArc(sketch, "E207", {"start": v(-176.4, -273.65) * mm, "mid": v(125.36, 0) * mm, "end": v(-176.4, 273.65) * mm});
            skSolve(sketch);
        }
        {
            var Q1;
            Q1 = qSketchRegion(id + "F149", true);
            var Q2;
            Q2 = qSketchRegion(id + "F152", true);
            loft(context, id + "F153", {"sheetProfilesArray" : [{ "sheetProfileEntities" : qUnion([Q1]) }, { "sheetProfileEntities" : qUnion([Q2]) }]});
        }
        {
            var Q0;
            Q0=qCreatedBy(id+"F148.planeOp",FACE);
            cPlane(context, id + "F154", {"entities" : qUnion([Q0]), "cplaneType" : CPlaneType.OFFSET, "offset" : 25 * mm, "width" : 150 * mm, "height" : 150 * mm});
        }
        {
            var Q0;
            Q0=qCreatedBy(id+"F154.planeOp",FACE);
            var sketch = newSketch(context, id + "F155", { "sketchPlane" : qUnion([Q0])});
            skLineSegment(sketch, "E208", {"start": v(-168.5, 227.12) * mm, "end": v(-171.41, 277.03) * mm});
            skLineSegment(sketch, "E209", {"start": v(-168.5, -227.12) * mm, "end": v(-171.41, -277.03) * mm});
            skArc(sketch, "E210", {"start": v(-168.5, -227.12) * mm, "mid": v(72.27, 0) * mm, "end": v(-168.5, 227.12) * mm});
            skArc(sketch, "E211", {"start": v(-171.41, -277.03) * mm, "mid": v(122.27, 0) * mm, "end": v(-171.41, 277.03) * mm});
            skSolve(sketch);
        }
        {
            var Q1;
            Q1 = qSketchRegion(id + "F152", true);
            var Q2;
            Q2 = qSketchRegion(id + "F155", true);
            loft(context, id + "F156", {"sheetProfilesArray" : [{ "sheetProfileEntities" : qUnion([Q1]) }, { "sheetProfileEntities" : qUnion([Q2]) }]});
        }
        {
            var Q0;
            Q0=qCreatedBy(id+"F151.planeOp",FACE);
            cPlane(context, id + "F157", {"entities" : qUnion([Q0]), "cplaneType" : CPlaneType.OFFSET, "offset" : 25 * mm, "width" : 150 * mm, "height" : 150 * mm});
        }
        {
            var Q0;
            Q0=qCreatedBy(id+"F157.planeOp",FACE);
            var sketch = newSketch(context, id + "F158", { "sketchPlane" : qUnion([Q0])});
            skLineSegment(sketch, "E212", {"start": v(-165.36, 230.21) * mm, "end": v(-166.28, 280.2) * mm});
            skLineSegment(sketch, "E213", {"start": v(-165.36, -230.21) * mm, "end": v(-166.28, -280.2) * mm});
            skArc(sketch, "E214", {"start": v(-165.36, -230.21) * mm, "mid": v(69.16, 0) * mm, "end": v(-165.36, 230.21) * mm});
            skArc(sketch, "E215", {"start": v(-166.28, -280.2) * mm, "mid": v(119.16, 0) * mm, "end": v(-166.28, 280.2) * mm});
            skSolve(sketch);
        }
        {
            var Q1;
            Q1 = qSketchRegion(id + "F155", true);
            var Q2;
            Q2 = qSketchRegion(id + "F158", true);
            loft(context, id + "F159", {"sheetProfilesArray" : [{ "sheetProfileEntities" : qUnion([Q1]) }, { "sheetProfileEntities" : qUnion([Q2]) }]});
        }
        {
            var Q0;
            Q0=qCreatedBy(id+"F154.planeOp",FACE);
            cPlane(context, id + "F160", {"entities" : qUnion([Q0]), "cplaneType" : CPlaneType.OFFSET, "offset" : 25 * mm, "width" : 150 * mm, "height" : 150 * mm});
        }
        {
            var Q0;
            Q0=qCreatedBy(id+"F160.planeOp",FACE);
            var sketch = newSketch(context, id + "F161", { "sketchPlane" : qUnion([Q0])});
            skLineSegment(sketch, "E216", {"start": v(-162.1, 233.16) * mm, "end": v(-161.02, 283.15) * mm});
            skLineSegment(sketch, "E217", {"start": v(-162.1, -233.16) * mm, "end": v(-161.02, -283.15) * mm});
            skArc(sketch, "E218", {"start": v(-162.1, -233.16) * mm, "mid": v(66.04, 0) * mm, "end": v(-162.1, 233.16) * mm});
            skArc(sketch, "E219", {"start": v(-161.02, -283.15) * mm, "mid": v(116.04, 0) * mm, "end": v(-161.02, 283.15) * mm});
            skSolve(sketch);
        }
        {
            var Q1;
            Q1 = qSketchRegion(id + "F158", true);
            var Q2;
            Q2 = qSketchRegion(id + "F161", true);
            loft(context, id + "F162", {"sheetProfilesArray" : [{ "sheetProfileEntities" : qUnion([Q1]) }, { "sheetProfileEntities" : qUnion([Q2]) }]});
        }
        {
            var Q0;
            Q0=qCreatedBy(id+"F157.planeOp",FACE);
            cPlane(context, id + "F163", {"entities" : qUnion([Q0]), "cplaneType" : CPlaneType.OFFSET, "offset" : 25 * mm, "width" : 150 * mm, "height" : 150 * mm});
        }
        {
            var Q0;
            Q0=qCreatedBy(id+"F163.planeOp",FACE);
            var sketch = newSketch(context, id + "F164", { "sketchPlane" : qUnion([Q0])});
            skLineSegment(sketch, "E220", {"start": v(-158.75, 235.95) * mm, "end": v(-155.64, 285.85) * mm});
            skLineSegment(sketch, "E221", {"start": v(-158.75, -235.95) * mm, "end": v(-155.64, -285.85) * mm});
            skArc(sketch, "E222", {"start": v(-158.75, -235.95) * mm, "mid": v(62.92, 0) * mm, "end": v(-158.75, 235.95) * mm});
            skArc(sketch, "E223", {"start": v(-155.64, -285.85) * mm, "mid": v(112.92, 0) * mm, "end": v(-155.64, 285.85) * mm});
            skSolve(sketch);
        }
        {
            var Q1;
            Q1 = qSketchRegion(id + "F161", true);
            var Q2;
            Q2 = qSketchRegion(id + "F164", true);
            loft(context, id + "F165", {"sheetProfilesArray" : [{ "sheetProfileEntities" : qUnion([Q1]) }, { "sheetProfileEntities" : qUnion([Q2]) }]});
        }
        {
            var Q0;
            Q0=qCreatedBy(id+"F160.planeOp",FACE);
            cPlane(context, id + "F166", {"entities" : qUnion([Q0]), "cplaneType" : CPlaneType.OFFSET, "offset" : 25 * mm, "width" : 150 * mm, "height" : 150 * mm});
        }
        {
            var Q0;
            Q0=qCreatedBy(id+"F166.planeOp",FACE);
            var sketch = newSketch(context, id + "F167", { "sketchPlane" : qUnion([Q0])});
            skLineSegment(sketch, "E224", {"start": v(-155.3, 238.56) * mm, "end": v(-150.14, 288.3) * mm});
            skLineSegment(sketch, "E225", {"start": v(-155.3, -238.56) * mm, "end": v(-150.14, -288.3) * mm});
            skArc(sketch, "E226", {"start": v(-155.3, -238.56) * mm, "mid": v(59.8, 0) * mm, "end": v(-155.3, 238.56) * mm});
            skArc(sketch, "E227", {"start": v(-150.14, -288.3) * mm, "mid": v(109.8, 0) * mm, "end": v(-150.14, 288.3) * mm});
            skSolve(sketch);
        }
        {
            var Q1;
            Q1 = qSketchRegion(id + "F164", true);
            var Q2;
            Q2 = qSketchRegion(id + "F167", true);
            loft(context, id + "F168", {"sheetProfilesArray" : [{ "sheetProfileEntities" : qUnion([Q1]) }, { "sheetProfileEntities" : qUnion([Q2]) }]});
        }
        {
            var Q0;
            Q0=qCreatedBy(id+"F163.planeOp",FACE);
            cPlane(context, id + "F169", {"entities" : qUnion([Q0]), "cplaneType" : CPlaneType.OFFSET, "offset" : 25 * mm, "width" : 150 * mm, "height" : 150 * mm});
        }
        {
            var Q0;
            Q0=qCreatedBy(id+"F169.planeOp",FACE);
            var sketch = newSketch(context, id + "F170", { "sketchPlane" : qUnion([Q0])});
            skLineSegment(sketch, "E228", {"start": v(-151.75, 240.98) * mm, "end": v(-144.54, 290.46) * mm});
            skLineSegment(sketch, "E229", {"start": v(-151.75, -240.98) * mm, "end": v(-144.54, -290.46) * mm});
            skArc(sketch, "E230", {"start": v(-151.75, -240.98) * mm, "mid": v(56.66, 0) * mm, "end": v(-151.75, 240.98) * mm});
            skArc(sketch, "E231", {"start": v(-144.54, -290.46) * mm, "mid": v(106.66, 0) * mm, "end": v(-144.54, 290.46) * mm});
            skSolve(sketch);
        }
        {
            var Q1;
            Q1 = qSketchRegion(id + "F167", true);
            var Q2;
            Q2 = qSketchRegion(id + "F170", true);
            loft(context, id + "F171", {"sheetProfilesArray" : [{ "sheetProfileEntities" : qUnion([Q1]) }, { "sheetProfileEntities" : qUnion([Q2]) }]});
        }
        {
            var Q0;
            Q0=qCreatedBy(id+"F166.planeOp",FACE);
            cPlane(context, id + "F172", {"entities" : qUnion([Q0]), "cplaneType" : CPlaneType.OFFSET, "offset" : 25 * mm, "width" : 150 * mm, "height" : 150 * mm});
        }
        {
            var Q0;
            Q0=qCreatedBy(id+"F172.planeOp",FACE);
            var sketch = newSketch(context, id + "F173", { "sketchPlane" : qUnion([Q0])});
            skLineSegment(sketch, "E232", {"start": v(-148.12, 243.2) * mm, "end": v(-138.86, 292.34) * mm});
            skLineSegment(sketch, "E233", {"start": v(-148.12, -243.2) * mm, "end": v(-138.86, -292.34) * mm});
            skArc(sketch, "E234", {"start": v(-148.12, -243.2) * mm, "mid": v(53.54, 0) * mm, "end": v(-148.12, 243.2) * mm});
            skArc(sketch, "E235", {"start": v(-138.86, -292.34) * mm, "mid": v(103.54, 0) * mm, "end": v(-138.86, 292.34) * mm});
            skSolve(sketch);
        }
        {
            var Q1;
            Q1 = qSketchRegion(id + "F170", true);
            var Q2;
            Q2 = qSketchRegion(id + "F173", true);
            loft(context, id + "F174", {"sheetProfilesArray" : [{ "sheetProfileEntities" : qUnion([Q1]) }, { "sheetProfileEntities" : qUnion([Q2]) }]});
        }
        {
            var Q0;
            Q0=qCreatedBy(id+"F169.planeOp",FACE);
            cPlane(context, id + "F175", {"entities" : qUnion([Q0]), "cplaneType" : CPlaneType.OFFSET, "offset" : 25 * mm, "width" : 150 * mm, "height" : 150 * mm});
        }
        {
            var Q0;
            Q0=qCreatedBy(id+"F175.planeOp",FACE);
            var sketch = newSketch(context, id + "F176", { "sketchPlane" : qUnion([Q0])});
            skLineSegment(sketch, "E236", {"start": v(-144.4, 245.2) * mm, "end": v(-133.1, 293.91) * mm});
            skLineSegment(sketch, "E237", {"start": v(-144.4, -245.2) * mm, "end": v(-133.1, -293.91) * mm});
            skArc(sketch, "E238", {"start": v(-144.4, -245.2) * mm, "mid": v(50.43, 0) * mm, "end": v(-144.4, 245.2) * mm});
            skArc(sketch, "E239", {"start": v(-133.1, -293.91) * mm, "mid": v(100.43, 0) * mm, "end": v(-133.1, 293.91) * mm});
            skSolve(sketch);
        }
        {
            var Q1;
            Q1 = qSketchRegion(id + "F173", true);
            var Q2;
            Q2 = qSketchRegion(id + "F176", true);
            loft(context, id + "F177", {"sheetProfilesArray" : [{ "sheetProfileEntities" : qUnion([Q1]) }, { "sheetProfileEntities" : qUnion([Q2]) }]});
        }
        {
            var Q0;
            Q0=qCreatedBy(id+"F172.planeOp",FACE);
            cPlane(context, id + "F178", {"entities" : qUnion([Q0]), "cplaneType" : CPlaneType.OFFSET, "offset" : 25 * mm, "width" : 150 * mm, "height" : 150 * mm});
        }
        {
            var Q0;
            Q0=qCreatedBy(id+"F178.planeOp",FACE);
            var sketch = newSketch(context, id + "F179", { "sketchPlane" : qUnion([Q0])});
            skLineSegment(sketch, "E240", {"start": v(-140.6, 246.98) * mm, "end": v(-127.28, 295.17) * mm});
            skLineSegment(sketch, "E241", {"start": v(-140.6, -246.98) * mm, "end": v(-127.28, -295.17) * mm});
            skArc(sketch, "E242", {"start": v(-140.6, -246.98) * mm, "mid": v(47.34, 0) * mm, "end": v(-140.6, 246.98) * mm});
            skArc(sketch, "E243", {"start": v(-127.28, -295.17) * mm, "mid": v(97.34, 0) * mm, "end": v(-127.28, 295.17) * mm});
            skSolve(sketch);
        }
        {
            var Q1;
            Q1 = qSketchRegion(id + "F176", true);
            var Q2;
            Q2 = qSketchRegion(id + "F179", true);
            loft(context, id + "F180", {"sheetProfilesArray" : [{ "sheetProfileEntities" : qUnion([Q1]) }, { "sheetProfileEntities" : qUnion([Q2]) }]});
        }
        {
            var Q0;
            Q0=qCreatedBy(id+"F175.planeOp",FACE);
            cPlane(context, id + "F181", {"entities" : qUnion([Q0]), "cplaneType" : CPlaneType.OFFSET, "offset" : 25 * mm, "width" : 150 * mm, "height" : 150 * mm});
        }
        {
            var Q0;
            Q0=qCreatedBy(id+"F181.planeOp",FACE);
            var sketch = newSketch(context, id + "F182", { "sketchPlane" : qUnion([Q0])});
            skLineSegment(sketch, "E244", {"start": v(-136.75, 248.51) * mm, "end": v(-121.42, 296.1) * mm});
            skLineSegment(sketch, "E245", {"start": v(-136.75, -248.51) * mm, "end": v(-121.42, -296.1) * mm});
            skArc(sketch, "E246", {"start": v(-136.75, -248.51) * mm, "mid": v(44.27, 0) * mm, "end": v(-136.75, 248.51) * mm});
            skArc(sketch, "E247", {"start": v(-121.42, -296.1) * mm, "mid": v(94.27, 0) * mm, "end": v(-121.42, 296.1) * mm});
            skSolve(sketch);
        }
        {
            var Q1;
            Q1 = qSketchRegion(id + "F179", true);
            var Q2;
            Q2 = qSketchRegion(id + "F182", true);
            loft(context, id + "F183", {"sheetProfilesArray" : [{ "sheetProfileEntities" : qUnion([Q1]) }, { "sheetProfileEntities" : qUnion([Q2]) }]});
        }
        {
            var Q0;
            Q0=qCreatedBy(id+"F178.planeOp",FACE);
            cPlane(context, id + "F184", {"entities" : qUnion([Q0]), "cplaneType" : CPlaneType.OFFSET, "offset" : 25 * mm, "width" : 150 * mm, "height" : 150 * mm});
        }
        {
            var Q0;
            Q0=qCreatedBy(id+"F184.planeOp",FACE);
            var sketch = newSketch(context, id + "F185", { "sketchPlane" : qUnion([Q0])});
            skLineSegment(sketch, "E248", {"start": v(-132.84, 249.8) * mm, "end": v(-115.53, 296.7) * mm});
            skLineSegment(sketch, "E249", {"start": v(-132.84, -249.8) * mm, "end": v(-115.53, -296.7) * mm});
            skArc(sketch, "E250", {"start": v(-132.84, -249.8) * mm, "mid": v(41.23, 0) * mm, "end": v(-132.84, 249.8) * mm});
            skArc(sketch, "E251", {"start": v(-115.53, -296.7) * mm, "mid": v(91.23, 0) * mm, "end": v(-115.53, 296.7) * mm});
            skSolve(sketch);
        }
        {
            var Q1;
            Q1 = qSketchRegion(id + "F182", true);
            var Q2;
            Q2 = qSketchRegion(id + "F185", true);
            loft(context, id + "F186", {"sheetProfilesArray" : [{ "sheetProfileEntities" : qUnion([Q1]) }, { "sheetProfileEntities" : qUnion([Q2]) }]});
        }
        {
            var Q0;
            Q0=qCreatedBy(id+"F181.planeOp",FACE);
            cPlane(context, id + "F187", {"entities" : qUnion([Q0]), "cplaneType" : CPlaneType.OFFSET, "offset" : 25 * mm, "width" : 150 * mm, "height" : 150 * mm});
        }
        {
            var Q0;
            Q0=qCreatedBy(id+"F187.planeOp",FACE);
            var sketch = newSketch(context, id + "F188", { "sketchPlane" : qUnion([Q0])});
            skLineSegment(sketch, "E252", {"start": v(-128.89, 250.82) * mm, "end": v(-109.63, 296.97) * mm});
            skLineSegment(sketch, "E253", {"start": v(-128.89, -250.82) * mm, "end": v(-109.63, -296.97) * mm});
            skArc(sketch, "E254", {"start": v(-128.89, -250.82) * mm, "mid": v(38.22, 0) * mm, "end": v(-128.89, 250.82) * mm});
            skArc(sketch, "E255", {"start": v(-109.63, -296.97) * mm, "mid": v(88.22, 0) * mm, "end": v(-109.63, 296.97) * mm});
            skSolve(sketch);
        }
        {
            var Q1;
            Q1 = qSketchRegion(id + "F185", true);
            var Q2;
            Q2 = qSketchRegion(id + "F188", true);
            loft(context, id + "F189", {"sheetProfilesArray" : [{ "sheetProfileEntities" : qUnion([Q1]) }, { "sheetProfileEntities" : qUnion([Q2]) }]});
        }
        {
            var Q0;
            Q0=qCreatedBy(id+"F184.planeOp",FACE);
            cPlane(context, id + "F190", {"entities" : qUnion([Q0]), "cplaneType" : CPlaneType.OFFSET, "offset" : 25 * mm, "width" : 150 * mm, "height" : 150 * mm});
        }
        {
            var Q0;
            Q0=qCreatedBy(id+"F190.planeOp",FACE);
            var sketch = newSketch(context, id + "F191", { "sketchPlane" : qUnion([Q0])});
            skLineSegment(sketch, "E256", {"start": v(-124.9, 251.58) * mm, "end": v(-103.74, 296.88) * mm});
            skLineSegment(sketch, "E257", {"start": v(-124.9, -251.58) * mm, "end": v(-103.74, -296.88) * mm});
            skArc(sketch, "E258", {"start": v(-124.9, -251.58) * mm, "mid": v(35.26, 0) * mm, "end": v(-124.9, 251.58) * mm});
            skArc(sketch, "E259", {"start": v(-103.74, -296.88) * mm, "mid": v(85.26, 0) * mm, "end": v(-103.74, 296.88) * mm});
            skSolve(sketch);
        }
        {
            var Q1;
            Q1 = qSketchRegion(id + "F188", true);
            var Q2;
            Q2 = qSketchRegion(id + "F191", true);
            loft(context, id + "F192", {"sheetProfilesArray" : [{ "sheetProfileEntities" : qUnion([Q1]) }, { "sheetProfileEntities" : qUnion([Q2]) }]});
        }
        {
            var Q0;
            Q0=qCreatedBy(id+"F187.planeOp",FACE);
            cPlane(context, id + "F193", {"entities" : qUnion([Q0]), "cplaneType" : CPlaneType.OFFSET, "offset" : 25 * mm, "width" : 150 * mm, "height" : 150 * mm});
        }
        {
            var Q0;
            Q0=qCreatedBy(id+"F193.planeOp",FACE);
            var sketch = newSketch(context, id + "F194", { "sketchPlane" : qUnion([Q0])});
            skLineSegment(sketch, "E260", {"start": v(-120.9, 252.06) * mm, "end": v(-97.88, 296.45) * mm});
            skLineSegment(sketch, "E261", {"start": v(-120.9, -252.06) * mm, "end": v(-97.88, -296.45) * mm});
            skArc(sketch, "E262", {"start": v(-120.9, -252.06) * mm, "mid": v(32.34, 0) * mm, "end": v(-120.9, 252.06) * mm});
            skArc(sketch, "E263", {"start": v(-97.88, -296.45) * mm, "mid": v(82.34, 0) * mm, "end": v(-97.88, 296.45) * mm});
            skSolve(sketch);
        }
        {
            var Q1;
            Q1 = qSketchRegion(id + "F191", true);
            var Q2;
            Q2 = qSketchRegion(id + "F194", true);
            loft(context, id + "F195", {"sheetProfilesArray" : [{ "sheetProfileEntities" : qUnion([Q1]) }, { "sheetProfileEntities" : qUnion([Q2]) }]});
        }
        {
            var Q0;
            Q0=qCreatedBy(id+"F190.planeOp",FACE);
            cPlane(context, id + "F196", {"entities" : qUnion([Q0]), "cplaneType" : CPlaneType.OFFSET, "offset" : 25 * mm, "width" : 150 * mm, "height" : 150 * mm});
        }
        {
            var Q0;
            Q0=qCreatedBy(id+"F196.planeOp",FACE);
            var sketch = newSketch(context, id + "F197", { "sketchPlane" : qUnion([Q0])});
            skLineSegment(sketch, "E264", {"start": v(-116.89, 252.27) * mm, "end": v(-92.07, 295.67) * mm});
            skLineSegment(sketch, "E265", {"start": v(-116.89, -252.27) * mm, "end": v(-92.07, -295.67) * mm});
            skArc(sketch, "E266", {"start": v(-116.89, -252.27) * mm, "mid": v(29.47, 0) * mm, "end": v(-116.89, 252.27) * mm});
            skArc(sketch, "E267", {"start": v(-92.07, -295.67) * mm, "mid": v(79.47, 0) * mm, "end": v(-92.07, 295.67) * mm});
            skSolve(sketch);
        }
        {
            var Q1;
            Q1 = qSketchRegion(id + "F194", true);
            var Q2;
            Q2 = qSketchRegion(id + "F197", true);
            loft(context, id + "F198", {"sheetProfilesArray" : [{ "sheetProfileEntities" : qUnion([Q1]) }, { "sheetProfileEntities" : qUnion([Q2]) }]});
        }
        {
            var Q0;
            Q0=qCreatedBy(id+"F193.planeOp",FACE);
            cPlane(context, id + "F199", {"entities" : qUnion([Q0]), "cplaneType" : CPlaneType.OFFSET, "offset" : 25 * mm, "width" : 150 * mm, "height" : 150 * mm});
        }
        {
            var Q0;
            Q0=qCreatedBy(id+"F199.planeOp",FACE);
            var sketch = newSketch(context, id + "F200", { "sketchPlane" : qUnion([Q0])});
            skLineSegment(sketch, "E268", {"start": v(-112.88, 252.2) * mm, "end": v(-86.32, 294.55) * mm});
            skLineSegment(sketch, "E269", {"start": v(-112.88, -252.2) * mm, "end": v(-86.32, -294.55) * mm});
            skArc(sketch, "E270", {"start": v(-112.88, -252.2) * mm, "mid": v(26.66, 0) * mm, "end": v(-112.88, 252.2) * mm});
            skArc(sketch, "E271", {"start": v(-86.32, -294.55) * mm, "mid": v(76.66, 0) * mm, "end": v(-86.32, 294.55) * mm});
            skSolve(sketch);
        }
        {
            var Q1;
            Q1 = qSketchRegion(id + "F197", true);
            var Q2;
            Q2 = qSketchRegion(id + "F200", true);
            loft(context, id + "F201", {"sheetProfilesArray" : [{ "sheetProfileEntities" : qUnion([Q1]) }, { "sheetProfileEntities" : qUnion([Q2]) }]});
        }
        {
            var Q0;
            Q0=qCreatedBy(id+"F196.planeOp",FACE);
            cPlane(context, id + "F202", {"entities" : qUnion([Q0]), "cplaneType" : CPlaneType.OFFSET, "offset" : 25 * mm, "width" : 150 * mm, "height" : 150 * mm});
        }
        {
            var Q0;
            Q0=qCreatedBy(id+"F202.planeOp",FACE);
            var sketch = newSketch(context, id + "F203", { "sketchPlane" : qUnion([Q0])});
            skLineSegment(sketch, "E272", {"start": v(-108.89, 251.83) * mm, "end": v(-80.64, 293.09) * mm});
            skLineSegment(sketch, "E273", {"start": v(-108.89, -251.83) * mm, "end": v(-80.64, -293.09) * mm});
            skArc(sketch, "E274", {"start": v(-108.89, -251.83) * mm, "mid": v(23.91, 0) * mm, "end": v(-108.89, 251.83) * mm});
            skArc(sketch, "E275", {"start": v(-80.64, -293.09) * mm, "mid": v(73.91, 0) * mm, "end": v(-80.64, 293.09) * mm});
            skSolve(sketch);
        }
        {
            var Q1;
            Q1 = qSketchRegion(id + "F200", true);
            var Q2;
            Q2 = qSketchRegion(id + "F203", true);
            loft(context, id + "F204", {"sheetProfilesArray" : [{ "sheetProfileEntities" : qUnion([Q1]) }, { "sheetProfileEntities" : qUnion([Q2]) }]});
        }
        {
            var Q0;
            Q0=qCreatedBy(id+"F199.planeOp",FACE);
            cPlane(context, id + "F205", {"entities" : qUnion([Q0]), "cplaneType" : CPlaneType.OFFSET, "offset" : 25 * mm, "width" : 150 * mm, "height" : 150 * mm});
        }
        {
            var Q0;
            Q0=qCreatedBy(id+"F205.planeOp",FACE);
            var sketch = newSketch(context, id + "F206", { "sketchPlane" : qUnion([Q0])});
            skLineSegment(sketch, "E276", {"start": v(-104.92, 251.18) * mm, "end": v(-75.07, 291.3) * mm});
            skLineSegment(sketch, "E277", {"start": v(-104.92, -251.18) * mm, "end": v(-75.07, -291.3) * mm});
            skArc(sketch, "E278", {"start": v(-104.92, -251.18) * mm, "mid": v(21.23, 0) * mm, "end": v(-104.92, 251.18) * mm});
            skArc(sketch, "E279", {"start": v(-75.07, -291.3) * mm, "mid": v(71.23, 0) * mm, "end": v(-75.07, 291.3) * mm});
            skSolve(sketch);
        }
        {
            var Q1;
            Q1 = qSketchRegion(id + "F203", true);
            var Q2;
            Q2 = qSketchRegion(id + "F206", true);
            loft(context, id + "F207", {"sheetProfilesArray" : [{ "sheetProfileEntities" : qUnion([Q1]) }, { "sheetProfileEntities" : qUnion([Q2]) }]});
        }
        {
            var Q0;
            Q0=qCreatedBy(id+"F202.planeOp",FACE);
            cPlane(context, id + "F208", {"entities" : qUnion([Q0]), "cplaneType" : CPlaneType.OFFSET, "offset" : 25 * mm, "width" : 150 * mm, "height" : 150 * mm});
        }
        {
            var Q0;
            Q0=qCreatedBy(id+"F208.planeOp",FACE);
            var sketch = newSketch(context, id + "F209", { "sketchPlane" : qUnion([Q0])});
            skLineSegment(sketch, "E280", {"start": v(-101, 250.26) * mm, "end": v(-69.6, 289.17) * mm});
            skLineSegment(sketch, "E281", {"start": v(-101, -250.26) * mm, "end": v(-69.6, -289.17) * mm});
            skArc(sketch, "E282", {"start": v(-101, -250.26) * mm, "mid": v(18.62, 0) * mm, "end": v(-101, 250.26) * mm});
            skArc(sketch, "E283", {"start": v(-69.6, -289.17) * mm, "mid": v(68.62, 0) * mm, "end": v(-69.6, 289.17) * mm});
            skSolve(sketch);
        }
        {
            var Q1;
            Q1 = qSketchRegion(id + "F206", true);
            var Q2;
            Q2 = qSketchRegion(id + "F209", true);
            loft(context, id + "F210", {"sheetProfilesArray" : [{ "sheetProfileEntities" : qUnion([Q1]) }, { "sheetProfileEntities" : qUnion([Q2]) }]});
        }
        {
            var Q0;
            Q0=qCreatedBy(id+"F205.planeOp",FACE);
            cPlane(context, id + "F211", {"entities" : qUnion([Q0]), "cplaneType" : CPlaneType.OFFSET, "offset" : 25 * mm, "width" : 150 * mm, "height" : 150 * mm});
        }
        {
            var Q0;
            Q0=qCreatedBy(id+"F211.planeOp",FACE);
            var sketch = newSketch(context, id + "F212", { "sketchPlane" : qUnion([Q0])});
            skLineSegment(sketch, "E284", {"start": v(-97.14, 249.05) * mm, "end": v(-64.27, 286.73) * mm});
            skLineSegment(sketch, "E285", {"start": v(-97.14, -249.05) * mm, "end": v(-64.27, -286.73) * mm});
            skArc(sketch, "E286", {"start": v(-97.14, -249.05) * mm, "mid": v(16.1, 0) * mm, "end": v(-97.14, 249.05) * mm});
            skArc(sketch, "E287", {"start": v(-64.27, -286.73) * mm, "mid": v(66.1, 0) * mm, "end": v(-64.27, 286.73) * mm});
            skSolve(sketch);
        }
        {
            var Q1;
            Q1 = qSketchRegion(id + "F209", true);
            var Q2;
            Q2 = qSketchRegion(id + "F212", true);
            loft(context, id + "F213", {"sheetProfilesArray" : [{ "sheetProfileEntities" : qUnion([Q1]) }, { "sheetProfileEntities" : qUnion([Q2]) }]});
        }
        {
            var Q0;
            Q0=qCreatedBy(id+"F208.planeOp",FACE);
            cPlane(context, id + "F214", {"entities" : qUnion([Q0]), "cplaneType" : CPlaneType.OFFSET, "offset" : 25 * mm, "width" : 150 * mm, "height" : 150 * mm});
        }
        {
            var Q0;
            Q0=qCreatedBy(id+"F214.planeOp",FACE);
            var sketch = newSketch(context, id + "F215", { "sketchPlane" : qUnion([Q0])});
            skLineSegment(sketch, "E288", {"start": v(-93.34, 247.58) * mm, "end": v(-59.07, 284) * mm});
            skLineSegment(sketch, "E289", {"start": v(-93.34, -247.58) * mm, "end": v(-59.07, -284) * mm});
            skArc(sketch, "E290", {"start": v(-93.34, -247.58) * mm, "mid": v(13.64, 0) * mm, "end": v(-93.34, 247.58) * mm});
            skArc(sketch, "E291", {"start": v(-59.07, -284) * mm, "mid": v(63.64, 0) * mm, "end": v(-59.07, 284) * mm});
            skSolve(sketch);
        }
        {
            var Q1;
            Q1 = qSketchRegion(id + "F212", true);
            var Q2;
            Q2 = qSketchRegion(id + "F215", true);
            loft(context, id + "F216", {"sheetProfilesArray" : [{ "sheetProfileEntities" : qUnion([Q1]) }, { "sheetProfileEntities" : qUnion([Q2]) }]});
        }
        {
            var Q0;
            Q0=qCreatedBy(id+"F211.planeOp",FACE);
            cPlane(context, id + "F217", {"entities" : qUnion([Q0]), "cplaneType" : CPlaneType.OFFSET, "offset" : 25 * mm, "width" : 150 * mm, "height" : 150 * mm});
        }
        {
            var Q0;
            Q0=qCreatedBy(id+"F217.planeOp",FACE);
            var sketch = newSketch(context, id + "F218", { "sketchPlane" : qUnion([Q0])});
            skLineSegment(sketch, "E292", {"start": v(-89.61, 245.84) * mm, "end": v(-54.03, 280.96) * mm});
            skLineSegment(sketch, "E293", {"start": v(-89.61, -245.84) * mm, "end": v(-54.03, -280.96) * mm});
            skArc(sketch, "E294", {"start": v(-89.61, -245.84) * mm, "mid": v(11.28, 0) * mm, "end": v(-89.61, 245.84) * mm});
            skArc(sketch, "E295", {"start": v(-54.03, -280.96) * mm, "mid": v(61.28, 0) * mm, "end": v(-54.03, 280.96) * mm});
            skSolve(sketch);
        }
        {
            var Q1;
            Q1 = qSketchRegion(id + "F215", true);
            var Q2;
            Q2 = qSketchRegion(id + "F218", true);
            loft(context, id + "F219", {"sheetProfilesArray" : [{ "sheetProfileEntities" : qUnion([Q1]) }, { "sheetProfileEntities" : qUnion([Q2]) }]});
        }
        {
            var Q0;
            Q0=qCreatedBy(id+"F214.planeOp",FACE);
            cPlane(context, id + "F220", {"entities" : qUnion([Q0]), "cplaneType" : CPlaneType.OFFSET, "offset" : 25 * mm, "width" : 150 * mm, "height" : 150 * mm});
        }
        {
            var Q0;
            Q0=qCreatedBy(id+"F220.planeOp",FACE);
            var sketch = newSketch(context, id + "F221", { "sketchPlane" : qUnion([Q0])});
            skLineSegment(sketch, "E296", {"start": v(-85.97, 243.84) * mm, "end": v(-49.14, 277.65) * mm});
            skLineSegment(sketch, "E297", {"start": v(-85.97, -243.84) * mm, "end": v(-49.14, -277.65) * mm});
            skArc(sketch, "E298", {"start": v(-85.97, -243.84) * mm, "mid": v(9, 0) * mm, "end": v(-85.97, 243.84) * mm});
            skArc(sketch, "E299", {"start": v(-49.14, -277.65) * mm, "mid": v(59, 0) * mm, "end": v(-49.14, 277.65) * mm});
            skSolve(sketch);
        }
        {
            var Q1;
            Q1 = qSketchRegion(id + "F218", true);
            var Q2;
            Q2 = qSketchRegion(id + "F221", true);
            loft(context, id + "F222", {"sheetProfilesArray" : [{ "sheetProfileEntities" : qUnion([Q1]) }, { "sheetProfileEntities" : qUnion([Q2]) }]});
        }
        {
            var Q0;
            Q0=qCreatedBy(id+"F217.planeOp",FACE);
            cPlane(context, id + "F223", {"entities" : qUnion([Q0]), "cplaneType" : CPlaneType.OFFSET, "offset" : 25 * mm, "width" : 150 * mm, "height" : 150 * mm});
        }
        {
            var Q0;
            Q0=qCreatedBy(id+"F223.planeOp",FACE);
            var sketch = newSketch(context, id + "F224", { "sketchPlane" : qUnion([Q0])});
            skLineSegment(sketch, "E300", {"start": v(-82.43, 241.58) * mm, "end": v(-44.43, 274.09) * mm});
            skLineSegment(sketch, "E301", {"start": v(-82.43, -241.58) * mm, "end": v(-44.43, -274.09) * mm});
            skArc(sketch, "E302", {"start": v(-82.43, -241.58) * mm, "mid": v(6.8, 0) * mm, "end": v(-82.43, 241.58) * mm});
            skArc(sketch, "E303", {"start": v(-44.43, -274.09) * mm, "mid": v(56.8, 0) * mm, "end": v(-44.43, 274.09) * mm});
            skSolve(sketch);
        }
        {
            var Q1;
            Q1 = qSketchRegion(id + "F221", true);
            var Q2;
            Q2 = qSketchRegion(id + "F224", true);
            loft(context, id + "F225", {"sheetProfilesArray" : [{ "sheetProfileEntities" : qUnion([Q1]) }, { "sheetProfileEntities" : qUnion([Q2]) }]});
        }
        {
            var Q0;
            Q0=qCreatedBy(id+"F220.planeOp",FACE);
            cPlane(context, id + "F226", {"entities" : qUnion([Q0]), "cplaneType" : CPlaneType.OFFSET, "offset" : 25 * mm, "width" : 150 * mm, "height" : 150 * mm});
        }
        {
            var Q0;
            Q0=qCreatedBy(id+"F226.planeOp",FACE);
            var sketch = newSketch(context, id + "F227", { "sketchPlane" : qUnion([Q0])});
            skLineSegment(sketch, "E304", {"start": v(-78.98, 239.1) * mm, "end": v(-39.9, 270.27) * mm});
            skLineSegment(sketch, "E305", {"start": v(-78.98, -239.1) * mm, "end": v(-39.9, -270.27) * mm});
            skArc(sketch, "E306", {"start": v(-78.98, -239.1) * mm, "mid": v(4.7, 0) * mm, "end": v(-78.98, 239.1) * mm});
            skArc(sketch, "E307", {"start": v(-39.9, -270.27) * mm, "mid": v(54.7, 0) * mm, "end": v(-39.9, 270.27) * mm});
            skSolve(sketch);
        }
        {
            var Q1;
            Q1 = qSketchRegion(id + "F224", true);
            var Q2;
            Q2 = qSketchRegion(id + "F227", true);
            loft(context, id + "F228", {"sheetProfilesArray" : [{ "sheetProfileEntities" : qUnion([Q1]) }, { "sheetProfileEntities" : qUnion([Q2]) }]});
        }
        {
            var Q0;
            Q0=qCreatedBy(id+"F223.planeOp",FACE);
            cPlane(context, id + "F229", {"entities" : qUnion([Q0]), "cplaneType" : CPlaneType.OFFSET, "offset" : 25 * mm, "width" : 150 * mm, "height" : 150 * mm});
        }
        {
            var Q0;
            Q0=qCreatedBy(id+"F229.planeOp",FACE);
            var sketch = newSketch(context, id + "F230", { "sketchPlane" : qUnion([Q0])});
            skLineSegment(sketch, "E308", {"start": v(-75.65, 236.37) * mm, "end": v(-35.54, 266.23) * mm});
            skLineSegment(sketch, "E309", {"start": v(-75.65, -236.37) * mm, "end": v(-35.54, -266.23) * mm});
            skArc(sketch, "E310", {"start": v(-75.65, -236.37) * mm, "mid": v(2.68, 0) * mm, "end": v(-75.65, 236.37) * mm});
            skArc(sketch, "E311", {"start": v(-35.54, -266.23) * mm, "mid": v(52.68, 0) * mm, "end": v(-35.54, 266.23) * mm});
            skSolve(sketch);
        }
        {
            var Q1;
            Q1 = qSketchRegion(id + "F227", true);
            var Q2;
            Q2 = qSketchRegion(id + "F230", true);
            loft(context, id + "F231", {"sheetProfilesArray" : [{ "sheetProfileEntities" : qUnion([Q1]) }, { "sheetProfileEntities" : qUnion([Q2]) }]});
        }
        {
            var Q0;
            Q0=qCreatedBy(id+"F226.planeOp",FACE);
            cPlane(context, id + "F232", {"entities" : qUnion([Q0]), "cplaneType" : CPlaneType.OFFSET, "offset" : 25 * mm, "width" : 150 * mm, "height" : 150 * mm});
        }
        {
            var Q0;
            Q0=qCreatedBy(id+"F232.planeOp",FACE);
            var sketch = newSketch(context, id + "F233", { "sketchPlane" : qUnion([Q0])});
            skLineSegment(sketch, "E312", {"start": v(-72.43, 233.43) * mm, "end": v(-31.38, 261.98) * mm});
            skLineSegment(sketch, "E313", {"start": v(-72.43, -233.43) * mm, "end": v(-31.38, -261.98) * mm});
            skArc(sketch, "E314", {"start": v(-72.43, -233.43) * mm, "mid": v(0.76, 0) * mm, "end": v(-72.43, 233.43) * mm});
            skArc(sketch, "E315", {"start": v(-31.38, -261.98) * mm, "mid": v(50.76, 0) * mm, "end": v(-31.38, 261.98) * mm});
            skSolve(sketch);
        }
        {
            var Q1;
            Q1 = qSketchRegion(id + "F230", true);
            var Q2;
            Q2 = qSketchRegion(id + "F233", true);
            loft(context, id + "F234", {"sheetProfilesArray" : [{ "sheetProfileEntities" : qUnion([Q1]) }, { "sheetProfileEntities" : qUnion([Q2]) }]});
        }
        {
            var Q0;
            Q0=qCreatedBy(id+"F229.planeOp",FACE);
            cPlane(context, id + "F235", {"entities" : qUnion([Q0]), "cplaneType" : CPlaneType.OFFSET, "offset" : 25 * mm, "width" : 150 * mm, "height" : 150 * mm});
        }
        {
            var Q0;
            Q0=qCreatedBy(id+"F235.planeOp",FACE);
            var sketch = newSketch(context, id + "F236", { "sketchPlane" : qUnion([Q0])});
            skLineSegment(sketch, "E316", {"start": v(-69.33, 230.28) * mm, "end": v(-27.4, 257.53) * mm});
            skLineSegment(sketch, "E317", {"start": v(-69.33, -230.28) * mm, "end": v(-27.4, -257.53) * mm});
            skArc(sketch, "E318", {"start": v(-69.33, -230.28) * mm, "mid": v(-1.07, 0) * mm, "end": v(-69.33, 230.28) * mm});
            skArc(sketch, "E319", {"start": v(-27.4, -257.53) * mm, "mid": v(48.93, 0) * mm, "end": v(-27.4, 257.53) * mm});
            skSolve(sketch);
        }
        {
            var Q1;
            Q1 = qSketchRegion(id + "F233", true);
            var Q2;
            Q2 = qSketchRegion(id + "F236", true);
            loft(context, id + "F237", {"sheetProfilesArray" : [{ "sheetProfileEntities" : qUnion([Q1]) }, { "sheetProfileEntities" : qUnion([Q2]) }]});
        }
        {
            var Q0;
            Q0=qCreatedBy(id+"F232.planeOp",FACE);
            cPlane(context, id + "F238", {"entities" : qUnion([Q0]), "cplaneType" : CPlaneType.OFFSET, "offset" : 25 * mm, "width" : 150 * mm, "height" : 150 * mm});
        }
        {
            var Q0;
            Q0=qCreatedBy(id+"F238.planeOp",FACE);
            var sketch = newSketch(context, id + "F239", { "sketchPlane" : qUnion([Q0])});
            skLineSegment(sketch, "E320", {"start": v(-66.35, 226.94) * mm, "end": v(-23.62, 252.9) * mm});
            skLineSegment(sketch, "E321", {"start": v(-66.35, -226.94) * mm, "end": v(-23.62, -252.9) * mm});
            skArc(sketch, "E322", {"start": v(-66.35, -226.94) * mm, "mid": v(-2.81, 0) * mm, "end": v(-66.35, 226.94) * mm});
            skArc(sketch, "E323", {"start": v(-23.62, -252.9) * mm, "mid": v(47.19, 0) * mm, "end": v(-23.62, 252.9) * mm});
            skSolve(sketch);
        }
        {
            var Q1;
            Q1 = qSketchRegion(id + "F236", true);
            var Q2;
            Q2 = qSketchRegion(id + "F239", true);
            loft(context, id + "F240", {"sheetProfilesArray" : [{ "sheetProfileEntities" : qUnion([Q1]) }, { "sheetProfileEntities" : qUnion([Q2]) }]});
        }
        {
            var Q0;
            Q0=qCreatedBy(id+"F235.planeOp",FACE);
            cPlane(context, id + "F241", {"entities" : qUnion([Q0]), "cplaneType" : CPlaneType.OFFSET, "offset" : 25 * mm, "width" : 150 * mm, "height" : 150 * mm});
        }
        {
            var Q0;
            Q0=qCreatedBy(id+"F241.planeOp",FACE);
            var sketch = newSketch(context, id + "F242", { "sketchPlane" : qUnion([Q0])});
            skLineSegment(sketch, "E324", {"start": v(-63.5, 223.41) * mm, "end": v(-20.03, 248.11) * mm});
            skLineSegment(sketch, "E325", {"start": v(-63.5, -223.41) * mm, "end": v(-20.03, -248.11) * mm});
            skArc(sketch, "E326", {"start": v(-63.5, -223.41) * mm, "mid": v(-4.46, 0) * mm, "end": v(-63.5, 223.41) * mm});
            skArc(sketch, "E327", {"start": v(-20.03, -248.11) * mm, "mid": v(45.54, 0) * mm, "end": v(-20.03, 248.11) * mm});
            skSolve(sketch);
        }
        {
            var Q1;
            Q1 = qSketchRegion(id + "F239", true);
            var Q2;
            Q2 = qSketchRegion(id + "F242", true);
            loft(context, id + "F243", {"sheetProfilesArray" : [{ "sheetProfileEntities" : qUnion([Q1]) }, { "sheetProfileEntities" : qUnion([Q2]) }]});
        }
        {
            var Q0;
            Q0=qCreatedBy(id+"F238.planeOp",FACE);
            cPlane(context, id + "F244", {"entities" : qUnion([Q0]), "cplaneType" : CPlaneType.OFFSET, "offset" : 25 * mm, "width" : 150 * mm, "height" : 150 * mm});
        }
        {
            var Q0;
            Q0=qCreatedBy(id+"F244.planeOp",FACE);
            var sketch = newSketch(context, id + "F245", { "sketchPlane" : qUnion([Q0])});
            skLineSegment(sketch, "E328", {"start": v(-60.78, 219.7) * mm, "end": v(-16.63, 243.17) * mm});
            skLineSegment(sketch, "E329", {"start": v(-60.78, -219.7) * mm, "end": v(-16.63, -243.17) * mm});
            skArc(sketch, "E330", {"start": v(-60.78, -219.7) * mm, "mid": v(-6.03, 0) * mm, "end": v(-60.78, 219.7) * mm});
            skArc(sketch, "E331", {"start": v(-16.63, -243.17) * mm, "mid": v(43.97, 0) * mm, "end": v(-16.63, 243.17) * mm});
            skSolve(sketch);
        }
        {
            var Q1;
            Q1 = qSketchRegion(id + "F242", true);
            var Q2;
            Q2 = qSketchRegion(id + "F245", true);
            loft(context, id + "F246", {"sheetProfilesArray" : [{ "sheetProfileEntities" : qUnion([Q1]) }, { "sheetProfileEntities" : qUnion([Q2]) }]});
        }
        {
            var Q0;
            Q0=qCreatedBy(id+"F241.planeOp",FACE);
            cPlane(context, id + "F247", {"entities" : qUnion([Q0]), "cplaneType" : CPlaneType.OFFSET, "offset" : 25 * mm, "width" : 150 * mm, "height" : 150 * mm});
        }
        {
            var Q0;
            Q0=qCreatedBy(id+"F247.planeOp",FACE);
            var sketch = newSketch(context, id + "F248", { "sketchPlane" : qUnion([Q0])});
            skLineSegment(sketch, "E332", {"start": v(-58.19, 215.84) * mm, "end": v(-13.41, 238.1) * mm});
            skLineSegment(sketch, "E333", {"start": v(-58.19, -215.84) * mm, "end": v(-13.41, -238.1) * mm});
            skArc(sketch, "E334", {"start": v(-58.19, -215.84) * mm, "mid": v(-7.5, 0) * mm, "end": v(-58.19, 215.84) * mm});
            skArc(sketch, "E335", {"start": v(-13.41, -238.1) * mm, "mid": v(42.5, 0) * mm, "end": v(-13.41, 238.1) * mm});
            skSolve(sketch);
        }
        {
            var Q1;
            Q1 = qSketchRegion(id + "F245", true);
            var Q2;
            Q2 = qSketchRegion(id + "F248", true);
            loft(context, id + "F249", {"sheetProfilesArray" : [{ "sheetProfileEntities" : qUnion([Q1]) }, { "sheetProfileEntities" : qUnion([Q2]) }]});
        }
        {
            var Q0;
            Q0=qCreatedBy(id+"F244.planeOp",FACE);
            cPlane(context, id + "F250", {"entities" : qUnion([Q0]), "cplaneType" : CPlaneType.OFFSET, "offset" : 25 * mm, "width" : 150 * mm, "height" : 150 * mm});
        }
        {
            var Q0;
            Q0=qCreatedBy(id+"F250.planeOp",FACE);
            var sketch = newSketch(context, id + "F251", { "sketchPlane" : qUnion([Q0])});
            skLineSegment(sketch, "E336", {"start": v(-55.72, 211.83) * mm, "end": v(-10.38, 232.9) * mm});
            skLineSegment(sketch, "E337", {"start": v(-55.72, -211.83) * mm, "end": v(-10.38, -232.9) * mm});
            skArc(sketch, "E338", {"start": v(-55.72, -211.83) * mm, "mid": v(-8.9, 0) * mm, "end": v(-55.72, 211.83) * mm});
            skArc(sketch, "E339", {"start": v(-10.38, -232.9) * mm, "mid": v(41.1, 0) * mm, "end": v(-10.38, 232.9) * mm});
            skSolve(sketch);
        }
        {
            var Q1;
            Q1 = qSketchRegion(id + "F248", true);
            var Q2;
            Q2 = qSketchRegion(id + "F251", true);
            loft(context, id + "F252", {"sheetProfilesArray" : [{ "sheetProfileEntities" : qUnion([Q1]) }, { "sheetProfileEntities" : qUnion([Q2]) }]});
        }
        {
            var Q0;
            Q0=qCreatedBy(id+"F247.planeOp",FACE);
            cPlane(context, id + "F253", {"entities" : qUnion([Q0]), "cplaneType" : CPlaneType.OFFSET, "offset" : 25 * mm, "width" : 150 * mm, "height" : 150 * mm});
        }
        {
            var Q0;
            Q0=qCreatedBy(id+"F253.planeOp",FACE);
            var sketch = newSketch(context, id + "F254", { "sketchPlane" : qUnion([Q0])});
            skLineSegment(sketch, "E340", {"start": v(-53.38, 207.67) * mm, "end": v(-7.53, 227.6) * mm});
            skLineSegment(sketch, "E341", {"start": v(-53.38, -207.67) * mm, "end": v(-7.53, -227.6) * mm});
            skArc(sketch, "E342", {"start": v(-53.38, -207.67) * mm, "mid": v(-10.2, 0) * mm, "end": v(-53.38, 207.67) * mm});
            skArc(sketch, "E343", {"start": v(-7.53, -227.6) * mm, "mid": v(39.8, 0) * mm, "end": v(-7.53, 227.6) * mm});
            skSolve(sketch);
        }
        {
            var Q1;
            Q1 = qSketchRegion(id + "F251", true);
            var Q2;
            Q2 = qSketchRegion(id + "F254", true);
            loft(context, id + "F255", {"sheetProfilesArray" : [{ "sheetProfileEntities" : qUnion([Q1]) }, { "sheetProfileEntities" : qUnion([Q2]) }]});
        }
        {
            var Q0;
            Q0=qCreatedBy(id+"F250.planeOp",FACE);
            cPlane(context, id + "F256", {"entities" : qUnion([Q0]), "cplaneType" : CPlaneType.OFFSET, "offset" : 25 * mm, "width" : 150 * mm, "height" : 150 * mm});
        }
        {
            var Q0;
            Q0=qCreatedBy(id+"F256.planeOp",FACE);
            var sketch = newSketch(context, id + "F257", { "sketchPlane" : qUnion([Q0])});
            skLineSegment(sketch, "E344", {"start": v(-51.17, 203.4) * mm, "end": v(-4.85, 222.21) * mm});
            skLineSegment(sketch, "E345", {"start": v(-51.17, -203.4) * mm, "end": v(-4.85, -222.21) * mm});
            skArc(sketch, "E346", {"start": v(-51.17, -203.4) * mm, "mid": v(-11.43, 0) * mm, "end": v(-51.17, 203.4) * mm});
            skArc(sketch, "E347", {"start": v(-4.85, -222.21) * mm, "mid": v(38.57, 0) * mm, "end": v(-4.85, 222.21) * mm});
            skSolve(sketch);
        }
        {
            var Q1;
            Q1 = qSketchRegion(id + "F254", true);
            var Q2;
            Q2 = qSketchRegion(id + "F257", true);
            loft(context, id + "F258", {"sheetProfilesArray" : [{ "sheetProfileEntities" : qUnion([Q1]) }, { "sheetProfileEntities" : qUnion([Q2]) }]});
        }
        {
            var Q0;
            Q0=qCreatedBy(id+"F253.planeOp",FACE);
            cPlane(context, id + "F259", {"entities" : qUnion([Q0]), "cplaneType" : CPlaneType.OFFSET, "offset" : 25 * mm, "width" : 150 * mm, "height" : 150 * mm});
        }
        {
            var Q0;
            Q0=qCreatedBy(id+"F259.planeOp",FACE);
            var sketch = newSketch(context, id + "F260", { "sketchPlane" : qUnion([Q0])});
            skLineSegment(sketch, "E348", {"start": v(-49.09, 198.99) * mm, "end": v(-2.34, 216.74) * mm});
            skLineSegment(sketch, "E349", {"start": v(-49.09, -198.99) * mm, "end": v(-2.34, -216.74) * mm});
            skArc(sketch, "E350", {"start": v(-49.09, -198.99) * mm, "mid": v(-12.58, 0) * mm, "end": v(-49.09, 198.99) * mm});
            skArc(sketch, "E351", {"start": v(-2.34, -216.74) * mm, "mid": v(37.42, 0) * mm, "end": v(-2.34, 216.74) * mm});
            skSolve(sketch);
        }
        {
            var Q1;
            Q1 = qSketchRegion(id + "F257", true);
            var Q2;
            Q2 = qSketchRegion(id + "F260", true);
            loft(context, id + "F261", {"sheetProfilesArray" : [{ "sheetProfileEntities" : qUnion([Q1]) }, { "sheetProfileEntities" : qUnion([Q2]) }]});
        }
        {
            var Q0;
            Q0=qCreatedBy(id+"F256.planeOp",FACE);
            cPlane(context, id + "F262", {"entities" : qUnion([Q0]), "cplaneType" : CPlaneType.OFFSET, "offset" : 25 * mm, "width" : 150 * mm, "height" : 150 * mm});
        }
        {
            var Q0;
            Q0=qCreatedBy(id+"F262.planeOp",FACE);
            var sketch = newSketch(context, id + "F263", { "sketchPlane" : qUnion([Q0])});
            skLineSegment(sketch, "E352", {"start": v(-47.12, 194.48) * mm, "end": v(0, 211.2) * mm});
            skLineSegment(sketch, "E353", {"start": v(-47.12, -194.48) * mm, "end": v(0, -211.2) * mm});
            skArc(sketch, "E354", {"start": v(-47.12, -194.48) * mm, "mid": v(-13.66, 0) * mm, "end": v(-47.12, 194.48) * mm});
            skArc(sketch, "E355", {"start": v(0, -211.2) * mm, "mid": v(36.34, 0) * mm, "end": v(0, 211.2) * mm});
            skSolve(sketch);
        }
        {
            var Q1;
            Q1 = qSketchRegion(id + "F260", true);
            var Q2;
            Q2 = qSketchRegion(id + "F263", true);
            loft(context, id + "F264", {"sheetProfilesArray" : [{ "sheetProfileEntities" : qUnion([Q1]) }, { "sheetProfileEntities" : qUnion([Q2]) }]});
        }
        {
            var Q0;
            Q0=qCreatedBy(id+"F259.planeOp",FACE);
            cPlane(context, id + "F265", {"entities" : qUnion([Q0]), "cplaneType" : CPlaneType.OFFSET, "offset" : 25 * mm, "width" : 150 * mm, "height" : 150 * mm});
        }
        {
            var Q0;
            Q0=qCreatedBy(id+"F265.planeOp",FACE);
            var sketch = newSketch(context, id + "F266", { "sketchPlane" : qUnion([Q0])});
            skLineSegment(sketch, "E356", {"start": v(-45.28, 189.86) * mm, "end": v(2.18, 205.58) * mm});
            skLineSegment(sketch, "E357", {"start": v(-45.28, -189.86) * mm, "end": v(2.18, -205.58) * mm});
            skArc(sketch, "E358", {"start": v(-45.28, -189.86) * mm, "mid": v(-14.66, 0) * mm, "end": v(-45.28, 189.86) * mm});
            skArc(sketch, "E359", {"start": v(2.18, -205.58) * mm, "mid": v(35.34, 0) * mm, "end": v(2.18, 205.58) * mm});
            skSolve(sketch);
        }
        {
            var Q1;
            Q1 = qSketchRegion(id + "F263", true);
            var Q2;
            Q2 = qSketchRegion(id + "F266", true);
            loft(context, id + "F267", {"sheetProfilesArray" : [{ "sheetProfileEntities" : qUnion([Q1]) }, { "sheetProfileEntities" : qUnion([Q2]) }]});
        }
        {
            var Q0;
            Q0=qCreatedBy(id+"F262.planeOp",FACE);
            cPlane(context, id + "F268", {"entities" : qUnion([Q0]), "cplaneType" : CPlaneType.OFFSET, "offset" : 25 * mm, "width" : 150 * mm, "height" : 150 * mm});
        }
        {
            var Q0;
            Q0=qCreatedBy(id+"F268.planeOp",FACE);
            var sketch = newSketch(context, id + "F269", { "sketchPlane" : qUnion([Q0])});
            skLineSegment(sketch, "E360", {"start": v(-43.55, 185.16) * mm, "end": v(4.22, 199.92) * mm});
            skLineSegment(sketch, "E361", {"start": v(-43.55, -185.16) * mm, "end": v(4.22, -199.92) * mm});
            skArc(sketch, "E362", {"start": v(-43.55, -185.16) * mm, "mid": v(-15.6, 0) * mm, "end": v(-43.55, 185.16) * mm});
            skArc(sketch, "E363", {"start": v(4.22, -199.92) * mm, "mid": v(34.4, 0) * mm, "end": v(4.22, 199.92) * mm});
            skSolve(sketch);
        }
        {
            var Q1;
            Q1 = qSketchRegion(id + "F266", true);
            var Q2;
            Q2 = qSketchRegion(id + "F269", true);
            loft(context, id + "F270", {"sheetProfilesArray" : [{ "sheetProfileEntities" : qUnion([Q1]) }, { "sheetProfileEntities" : qUnion([Q2]) }]});
        }
        {
            var Q0;
            Q0=qCreatedBy(id+"F265.planeOp",FACE);
            cPlane(context, id + "F271", {"entities" : qUnion([Q0]), "cplaneType" : CPlaneType.OFFSET, "offset" : 25 * mm, "width" : 150 * mm, "height" : 150 * mm});
        }
        {
            var Q0;
            Q0=qCreatedBy(id+"F271.planeOp",FACE);
            var sketch = newSketch(context, id + "F272", { "sketchPlane" : qUnion([Q0])});
            skLineSegment(sketch, "E364", {"start": v(-41.93, 180.37) * mm, "end": v(6.11, 194.21) * mm});
            skLineSegment(sketch, "E365", {"start": v(-41.93, -180.37) * mm, "end": v(6.11, -194.21) * mm});
            skArc(sketch, "E366", {"start": v(-41.93, -180.37) * mm, "mid": v(-16.47, 0) * mm, "end": v(-41.93, 180.37) * mm});
            skArc(sketch, "E367", {"start": v(6.11, -194.21) * mm, "mid": v(33.53, 0) * mm, "end": v(6.11, 194.21) * mm});
            skSolve(sketch);
        }
        {
            var Q1;
            Q1 = qSketchRegion(id + "F269", true);
            var Q2;
            Q2 = qSketchRegion(id + "F272", true);
            loft(context, id + "F273", {"sheetProfilesArray" : [{ "sheetProfileEntities" : qUnion([Q1]) }, { "sheetProfileEntities" : qUnion([Q2]) }]});
        }
        {
            var Q0;
            Q0=qCreatedBy(id+"F268.planeOp",FACE);
            cPlane(context, id + "F274", {"entities" : qUnion([Q0]), "cplaneType" : CPlaneType.OFFSET, "offset" : 25 * mm, "width" : 150 * mm, "height" : 150 * mm});
        }
        {
            var Q0;
            Q0=qCreatedBy(id+"F274.planeOp",FACE);
            var sketch = newSketch(context, id + "F275", { "sketchPlane" : qUnion([Q0])});
            skLineSegment(sketch, "E368", {"start": v(-40.42, 175.5) * mm, "end": v(7.86, 188.47) * mm});
            skLineSegment(sketch, "E369", {"start": v(-40.42, -175.5) * mm, "end": v(7.86, -188.47) * mm});
            skArc(sketch, "E370", {"start": v(-40.42, -175.5) * mm, "mid": v(-17.27, 0) * mm, "end": v(-40.42, 175.5) * mm});
            skArc(sketch, "E371", {"start": v(7.86, -188.47) * mm, "mid": v(32.73, 0) * mm, "end": v(7.86, 188.47) * mm});
            skSolve(sketch);
        }
        {
            var Q1;
            Q1 = qSketchRegion(id + "F272", true);
            var Q2;
            Q2 = qSketchRegion(id + "F275", true);
            loft(context, id + "F276", {"sheetProfilesArray" : [{ "sheetProfileEntities" : qUnion([Q1]) }, { "sheetProfileEntities" : qUnion([Q2]) }]});
        }
        {
            var Q0;
            Q0=qCreatedBy(id+"F271.planeOp",FACE);
            cPlane(context, id + "F277", {"entities" : qUnion([Q0]), "cplaneType" : CPlaneType.OFFSET, "offset" : 25 * mm, "width" : 150 * mm, "height" : 150 * mm});
        }
        {
            var Q0;
            Q0=qCreatedBy(id+"F277.planeOp",FACE);
            var sketch = newSketch(context, id + "F278", { "sketchPlane" : qUnion([Q0])});
            skLineSegment(sketch, "E372", {"start": v(-39.02, 170.56) * mm, "end": v(9.49, 182.7) * mm});
            skLineSegment(sketch, "E373", {"start": v(-39.02, -170.56) * mm, "end": v(9.49, -182.7) * mm});
            skArc(sketch, "E374", {"start": v(-39.02, -170.56) * mm, "mid": v(-18.02, 0) * mm, "end": v(-39.02, 170.56) * mm});
            skArc(sketch, "E375", {"start": v(9.49, -182.7) * mm, "mid": v(31.98, 0) * mm, "end": v(9.49, 182.7) * mm});
            skSolve(sketch);
        }
        {
            var Q1;
            Q1 = qSketchRegion(id + "F275", true);
            var Q2;
            Q2 = qSketchRegion(id + "F278", true);
            loft(context, id + "F279", {"sheetProfilesArray" : [{ "sheetProfileEntities" : qUnion([Q1]) }, { "sheetProfileEntities" : qUnion([Q2]) }]});
        }
        {
            var Q0;
            Q0=qCreatedBy(id+"F274.planeOp",FACE);
            cPlane(context, id + "F280", {"entities" : qUnion([Q0]), "cplaneType" : CPlaneType.OFFSET, "offset" : 25 * mm, "width" : 150 * mm, "height" : 150 * mm});
        }
        {
            var Q0;
            Q0=qCreatedBy(id+"F280.planeOp",FACE);
            var sketch = newSketch(context, id + "F281", { "sketchPlane" : qUnion([Q0])});
            skLineSegment(sketch, "E376", {"start": v(-37.71, 165.56) * mm, "end": v(10.99, 176.89) * mm});
            skLineSegment(sketch, "E377", {"start": v(-37.71, -165.56) * mm, "end": v(10.99, -176.89) * mm});
            skArc(sketch, "E378", {"start": v(-37.71, -165.56) * mm, "mid": v(-18.71, 0) * mm, "end": v(-37.71, 165.56) * mm});
            skArc(sketch, "E379", {"start": v(10.99, -176.89) * mm, "mid": v(31.29, 0) * mm, "end": v(10.99, 176.89) * mm});
            skSolve(sketch);
        }
        {
            var Q1;
            Q1 = qSketchRegion(id + "F278", true);
            var Q2;
            Q2 = qSketchRegion(id + "F281", true);
            loft(context, id + "F282", {"sheetProfilesArray" : [{ "sheetProfileEntities" : qUnion([Q1]) }, { "sheetProfileEntities" : qUnion([Q2]) }]});
        }
        {
            var Q0;
            Q0=qCreatedBy(id+"F277.planeOp",FACE);
            cPlane(context, id + "F283", {"entities" : qUnion([Q0]), "cplaneType" : CPlaneType.OFFSET, "offset" : 25 * mm, "width" : 150 * mm, "height" : 150 * mm});
        }
        {
            var Q0;
            Q0=qCreatedBy(id+"F283.planeOp",FACE);
            var sketch = newSketch(context, id + "F284", { "sketchPlane" : qUnion([Q0])});
            skLineSegment(sketch, "E380", {"start": v(-36.5, 160.5) * mm, "end": v(12.37, 171.07) * mm});
            skLineSegment(sketch, "E381", {"start": v(-36.5, -160.5) * mm, "end": v(12.37, -171.07) * mm});
            skArc(sketch, "E382", {"start": v(-36.5, -160.5) * mm, "mid": v(-19.35, 0) * mm, "end": v(-36.5, 160.5) * mm});
            skArc(sketch, "E383", {"start": v(12.37, -171.07) * mm, "mid": v(30.65, 0) * mm, "end": v(12.37, 171.07) * mm});
            skSolve(sketch);
        }
        {
            var Q1;
            Q1 = qSketchRegion(id + "F281", true);
            var Q2;
            Q2 = qSketchRegion(id + "F284", true);
            loft(context, id + "F285", {"sheetProfilesArray" : [{ "sheetProfileEntities" : qUnion([Q1]) }, { "sheetProfileEntities" : qUnion([Q2]) }]});
        }
        {
            var Q0;
            Q0=qCreatedBy(id+"F280.planeOp",FACE);
            cPlane(context, id + "F286", {"entities" : qUnion([Q0]), "cplaneType" : CPlaneType.OFFSET, "offset" : 25 * mm, "width" : 150 * mm, "height" : 150 * mm});
        }
        {
            var Q0;
            Q0=qCreatedBy(id+"F286.planeOp",FACE);
            var sketch = newSketch(context, id + "F287", { "sketchPlane" : qUnion([Q0])});
            skLineSegment(sketch, "E384", {"start": v(-35.38, 155.4) * mm, "end": v(13.65, 165.23) * mm});
            skLineSegment(sketch, "E385", {"start": v(-35.38, -155.4) * mm, "end": v(13.65, -165.23) * mm});
            skArc(sketch, "E386", {"start": v(-35.38, -155.4) * mm, "mid": v(-19.94, 0) * mm, "end": v(-35.38, 155.4) * mm});
            skArc(sketch, "E387", {"start": v(13.65, -165.23) * mm, "mid": v(30.06, 0) * mm, "end": v(13.65, 165.23) * mm});
            skSolve(sketch);
        }
        {
            var Q1;
            Q1 = qSketchRegion(id + "F284", true);
            var Q2;
            Q2 = qSketchRegion(id + "F287", true);
            loft(context, id + "F288", {"sheetProfilesArray" : [{ "sheetProfileEntities" : qUnion([Q1]) }, { "sheetProfileEntities" : qUnion([Q2]) }]});
        }
        {
            var Q0;
            Q0=qCreatedBy(id+"F283.planeOp",FACE);
            cPlane(context, id + "F289", {"entities" : qUnion([Q0]), "cplaneType" : CPlaneType.OFFSET, "offset" : 25 * mm, "width" : 150 * mm, "height" : 150 * mm});
        }
        {
            var Q0;
            Q0=qCreatedBy(id+"F289.planeOp",FACE);
            var sketch = newSketch(context, id + "F290", { "sketchPlane" : qUnion([Q0])});
            skLineSegment(sketch, "E388", {"start": v(-34.34, 150.23) * mm, "end": v(14.82, 159.38) * mm});
            skLineSegment(sketch, "E389", {"start": v(-34.34, -150.23) * mm, "end": v(14.82, -159.38) * mm});
            skArc(sketch, "E390", {"start": v(-34.34, -150.23) * mm, "mid": v(-20.48, 0) * mm, "end": v(-34.34, 150.23) * mm});
            skArc(sketch, "E391", {"start": v(14.82, -159.38) * mm, "mid": v(29.52, 0) * mm, "end": v(14.82, 159.38) * mm});
            skSolve(sketch);
        }
        {
            var Q1;
            Q1 = qSketchRegion(id + "F287", true);
            var Q2;
            Q2 = qSketchRegion(id + "F290", true);
            loft(context, id + "F291", {"sheetProfilesArray" : [{ "sheetProfileEntities" : qUnion([Q1]) }, { "sheetProfileEntities" : qUnion([Q2]) }]});
        }
        {
            var Q0;
            Q0=qCreatedBy(id+"F286.planeOp",FACE);
            cPlane(context, id + "F292", {"entities" : qUnion([Q0]), "cplaneType" : CPlaneType.OFFSET, "offset" : 25 * mm, "width" : 150 * mm, "height" : 150 * mm});
        }
        {
            var Q0;
            Q0=qCreatedBy(id+"F292.planeOp",FACE);
            var sketch = newSketch(context, id + "F293", { "sketchPlane" : qUnion([Q0])});
            skLineSegment(sketch, "E392", {"start": v(-33.38, 145.02) * mm, "end": v(15.9, 153.52) * mm});
            skLineSegment(sketch, "E393", {"start": v(-33.38, -145.02) * mm, "end": v(15.9, -153.52) * mm});
            skArc(sketch, "E394", {"start": v(-33.38, -145.02) * mm, "mid": v(-20.98, 0) * mm, "end": v(-33.38, 145.02) * mm});
            skArc(sketch, "E395", {"start": v(15.9, -153.52) * mm, "mid": v(29.02, 0) * mm, "end": v(15.9, 153.52) * mm});
            skSolve(sketch);
        }
        {
            var Q1;
            Q1 = qSketchRegion(id + "F290", true);
            var Q2;
            Q2 = qSketchRegion(id + "F293", true);
            loft(context, id + "F294", {"sheetProfilesArray" : [{ "sheetProfileEntities" : qUnion([Q1]) }, { "sheetProfileEntities" : qUnion([Q2]) }]});
        }
        {
            var Q0;
            Q0=qCreatedBy(id+"F289.planeOp",FACE);
            cPlane(context, id + "F295", {"entities" : qUnion([Q0]), "cplaneType" : CPlaneType.OFFSET, "offset" : 25 * mm, "width" : 150 * mm, "height" : 150 * mm});
        }
        {
            var Q0;
            Q0=qCreatedBy(id+"F295.planeOp",FACE);
            var sketch = newSketch(context, id + "F296", { "sketchPlane" : qUnion([Q0])});
            skLineSegment(sketch, "E396", {"start": v(-32.5, 139.78) * mm, "end": v(16.88, 147.65) * mm});
            skLineSegment(sketch, "E397", {"start": v(-32.5, -139.78) * mm, "end": v(16.88, -147.65) * mm});
            skArc(sketch, "E398", {"start": v(-32.5, -139.78) * mm, "mid": v(-21.43, 0) * mm, "end": v(-32.5, 139.78) * mm});
            skArc(sketch, "E399", {"start": v(16.88, -147.65) * mm, "mid": v(28.57, 0) * mm, "end": v(16.88, 147.65) * mm});
            skSolve(sketch);
        }
        {
            var Q1;
            Q1 = qSketchRegion(id + "F293", true);
            var Q2;
            Q2 = qSketchRegion(id + "F296", true);
            loft(context, id + "F297", {"sheetProfilesArray" : [{ "sheetProfileEntities" : qUnion([Q1]) }, { "sheetProfileEntities" : qUnion([Q2]) }]});
        }
        {
            var Q0;
            Q0=qCreatedBy(id+"F292.planeOp",FACE);
            cPlane(context, id + "F298", {"entities" : qUnion([Q0]), "cplaneType" : CPlaneType.OFFSET, "offset" : 25 * mm, "width" : 150 * mm, "height" : 150 * mm});
        }
        {
            var Q0;
            Q0=qCreatedBy(id+"F298.planeOp",FACE);
            var sketch = newSketch(context, id + "F299", { "sketchPlane" : qUnion([Q0])});
            skLineSegment(sketch, "E400", {"start": v(-31.7, 134.5) * mm, "end": v(17.77, 141.78) * mm});
            skLineSegment(sketch, "E401", {"start": v(-31.7, -134.5) * mm, "end": v(17.77, -141.78) * mm});
            skArc(sketch, "E402", {"start": v(-31.7, -134.5) * mm, "mid": v(-21.84, 0) * mm, "end": v(-31.7, 134.5) * mm});
            skArc(sketch, "E403", {"start": v(17.77, -141.78) * mm, "mid": v(28.16, 0) * mm, "end": v(17.77, 141.78) * mm});
            skSolve(sketch);
        }
        {
            var Q1;
            Q1 = qSketchRegion(id + "F296", true);
            var Q2;
            Q2 = qSketchRegion(id + "F299", true);
            loft(context, id + "F300", {"sheetProfilesArray" : [{ "sheetProfileEntities" : qUnion([Q1]) }, { "sheetProfileEntities" : qUnion([Q2]) }]});
        }
        {
            var Q0;
            Q0=qCreatedBy(id+"F295.planeOp",FACE);
            cPlane(context, id + "F301", {"entities" : qUnion([Q0]), "cplaneType" : CPlaneType.OFFSET, "offset" : 25 * mm, "width" : 150 * mm, "height" : 150 * mm});
        }
        {
            var Q0;
            Q0=qCreatedBy(id+"F301.planeOp",FACE);
            var sketch = newSketch(context, id + "F302", { "sketchPlane" : qUnion([Q0])});
            skLineSegment(sketch, "E404", {"start": v(-30.95, 129.19) * mm, "end": v(18.6, 135.91) * mm});
            skLineSegment(sketch, "E405", {"start": v(-30.95, -129.19) * mm, "end": v(18.6, -135.91) * mm});
            skArc(sketch, "E406", {"start": v(-30.95, -129.19) * mm, "mid": v(-22.22, 0) * mm, "end": v(-30.95, 129.19) * mm});
            skArc(sketch, "E407", {"start": v(18.6, -135.91) * mm, "mid": v(27.78, 0) * mm, "end": v(18.6, 135.91) * mm});
            skSolve(sketch);
        }
        {
            var Q1;
            Q1 = qSketchRegion(id + "F299", true);
            var Q2;
            Q2 = qSketchRegion(id + "F302", true);
            loft(context, id + "F303", {"sheetProfilesArray" : [{ "sheetProfileEntities" : qUnion([Q1]) }, { "sheetProfileEntities" : qUnion([Q2]) }]});
        }
        {
            var Q0;
            Q0=qCreatedBy(id+"F298.planeOp",FACE);
            cPlane(context, id + "F304", {"entities" : qUnion([Q0]), "cplaneType" : CPlaneType.OFFSET, "offset" : 25 * mm, "width" : 150 * mm, "height" : 150 * mm});
        }
        {
            var Q0;
            Q0=qCreatedBy(id+"F304.planeOp",FACE);
            var sketch = newSketch(context, id + "F305", { "sketchPlane" : qUnion([Q0])});
            skLineSegment(sketch, "E408", {"start": v(-30.28, 123.84) * mm, "end": v(19.34, 130.04) * mm});
            skLineSegment(sketch, "E409", {"start": v(-30.28, -123.84) * mm, "end": v(19.34, -130.04) * mm});
            skArc(sketch, "E410", {"start": v(-30.28, -123.84) * mm, "mid": v(-22.57, 0) * mm, "end": v(-30.28, 123.84) * mm});
            skArc(sketch, "E411", {"start": v(19.34, -130.04) * mm, "mid": v(27.43, 0) * mm, "end": v(19.34, 130.04) * mm});
            skSolve(sketch);
        }
        {
            var Q1;
            Q1 = qSketchRegion(id + "F302", true);
            var Q2;
            Q2 = qSketchRegion(id + "F305", true);
            loft(context, id + "F306", {"sheetProfilesArray" : [{ "sheetProfileEntities" : qUnion([Q1]) }, { "sheetProfileEntities" : qUnion([Q2]) }]});
        }
        {
            var Q0;
            Q0=qCreatedBy(id+"F301.planeOp",FACE);
            cPlane(context, id + "F307", {"entities" : qUnion([Q0]), "cplaneType" : CPlaneType.OFFSET, "offset" : 25 * mm, "width" : 150 * mm, "height" : 150 * mm});
        }
        {
            var Q0;
            Q0=qCreatedBy(id+"F307.planeOp",FACE);
            var sketch = newSketch(context, id + "F308", { "sketchPlane" : qUnion([Q0])});
            skLineSegment(sketch, "E412", {"start": v(-29.66, 118.47) * mm, "end": v(20.01, 124.18) * mm});
            skLineSegment(sketch, "E413", {"start": v(-29.66, -118.47) * mm, "end": v(20.01, -124.18) * mm});
            skArc(sketch, "E414", {"start": v(-29.66, -118.47) * mm, "mid": v(-22.88, 0) * mm, "end": v(-29.66, 118.47) * mm});
            skArc(sketch, "E415", {"start": v(20.01, -124.18) * mm, "mid": v(27.12, 0) * mm, "end": v(20.01, 124.18) * mm});
            skSolve(sketch);
        }
        {
            var Q1;
            Q1 = qSketchRegion(id + "F305", true);
            var Q2;
            Q2 = qSketchRegion(id + "F308", true);
            loft(context, id + "F309", {"sheetProfilesArray" : [{ "sheetProfileEntities" : qUnion([Q1]) }, { "sheetProfileEntities" : qUnion([Q2]) }]});
        }
        {
            var Q0;
            Q0=qCreatedBy(id+"F304.planeOp",FACE);
            cPlane(context, id + "F310", {"entities" : qUnion([Q0]), "cplaneType" : CPlaneType.OFFSET, "offset" : 25 * mm, "width" : 150 * mm, "height" : 150 * mm});
        }
        {
            var Q0;
            Q0=qCreatedBy(id+"F310.planeOp",FACE);
            var sketch = newSketch(context, id + "F311", { "sketchPlane" : qUnion([Q0])});
            skLineSegment(sketch, "E416", {"start": v(-29.1, 113.08) * mm, "end": v(20.63, 118.31) * mm});
            skLineSegment(sketch, "E417", {"start": v(-29.1, -113.08) * mm, "end": v(20.63, -118.31) * mm});
            skArc(sketch, "E418", {"start": v(-29.1, -113.08) * mm, "mid": v(-23.16, 0) * mm, "end": v(-29.1, 113.08) * mm});
            skArc(sketch, "E419", {"start": v(20.63, -118.31) * mm, "mid": v(26.84, 0) * mm, "end": v(20.63, 118.31) * mm});
            skSolve(sketch);
        }
        {
            var Q1;
            Q1 = qSketchRegion(id + "F308", true);
            var Q2;
            Q2 = qSketchRegion(id + "F311", true);
            loft(context, id + "F312", {"sheetProfilesArray" : [{ "sheetProfileEntities" : qUnion([Q1]) }, { "sheetProfileEntities" : qUnion([Q2]) }]});
        }
        {
            var Q0;
            Q0=qCreatedBy(id+"F307.planeOp",FACE);
            cPlane(context, id + "F313", {"entities" : qUnion([Q0]), "cplaneType" : CPlaneType.OFFSET, "offset" : 25 * mm, "width" : 150 * mm, "height" : 150 * mm});
        }
        {
            var Q0;
            Q0=qCreatedBy(id+"F313.planeOp",FACE);
            var sketch = newSketch(context, id + "F314", { "sketchPlane" : qUnion([Q0])});
            skLineSegment(sketch, "E420", {"start": v(-28.59, 107.66) * mm, "end": v(21.18, 112.45) * mm});
            skLineSegment(sketch, "E421", {"start": v(-28.59, -107.66) * mm, "end": v(21.18, -112.45) * mm});
            skArc(sketch, "E422", {"start": v(-28.59, -107.66) * mm, "mid": v(-23.42, 0) * mm, "end": v(-28.59, 107.66) * mm});
            skArc(sketch, "E423", {"start": v(21.18, -112.45) * mm, "mid": v(26.58, 0) * mm, "end": v(21.18, 112.45) * mm});
            skSolve(sketch);
        }
        {
            var Q1;
            Q1 = qSketchRegion(id + "F311", true);
            var Q2;
            Q2 = qSketchRegion(id + "F314", true);
            loft(context, id + "F315", {"sheetProfilesArray" : [{ "sheetProfileEntities" : qUnion([Q1]) }, { "sheetProfileEntities" : qUnion([Q2]) }]});
        }
        {
            var Q0;
            Q0=qCreatedBy(id+"F310.planeOp",FACE);
            cPlane(context, id + "F316", {"entities" : qUnion([Q0]), "cplaneType" : CPlaneType.OFFSET, "offset" : 25 * mm, "width" : 150 * mm, "height" : 150 * mm});
        }
        {
            var Q0;
            Q0=qCreatedBy(id+"F316.planeOp",FACE);
            var sketch = newSketch(context, id + "F317", { "sketchPlane" : qUnion([Q0])});
            skLineSegment(sketch, "E424", {"start": v(-28.13, 102.22) * mm, "end": v(21.68, 106.6) * mm});
            skLineSegment(sketch, "E425", {"start": v(-28.13, -102.22) * mm, "end": v(21.68, -106.6) * mm});
            skArc(sketch, "E426", {"start": v(-28.13, -102.22) * mm, "mid": v(-23.65, 0) * mm, "end": v(-28.13, 102.22) * mm});
            skArc(sketch, "E427", {"start": v(21.68, -106.6) * mm, "mid": v(26.35, 0) * mm, "end": v(21.68, 106.6) * mm});
            skSolve(sketch);
        }
        {
            var Q1;
            Q1 = qSketchRegion(id + "F314", true);
            var Q2;
            Q2 = qSketchRegion(id + "F317", true);
            loft(context, id + "F318", {"sheetProfilesArray" : [{ "sheetProfileEntities" : qUnion([Q1]) }, { "sheetProfileEntities" : qUnion([Q2]) }]});
        }
        {
            var Q0;
            Q0=qCreatedBy(id+"F313.planeOp",FACE);
            cPlane(context, id + "F319", {"entities" : qUnion([Q0]), "cplaneType" : CPlaneType.OFFSET, "offset" : 25 * mm, "width" : 150 * mm, "height" : 150 * mm});
        }
        {
            var Q0;
            Q0=qCreatedBy(id+"F319.planeOp",FACE);
            var sketch = newSketch(context, id + "F320", { "sketchPlane" : qUnion([Q0])});
            skLineSegment(sketch, "E428", {"start": v(-27.72, 96.77) * mm, "end": v(22.13, 100.75) * mm});
            skLineSegment(sketch, "E429", {"start": v(-27.72, -96.77) * mm, "end": v(22.13, -100.75) * mm});
            skArc(sketch, "E430", {"start": v(-27.72, -96.77) * mm, "mid": v(-23.85, 0) * mm, "end": v(-27.72, 96.77) * mm});
            skArc(sketch, "E431", {"start": v(22.13, -100.75) * mm, "mid": v(26.15, 0) * mm, "end": v(22.13, 100.75) * mm});
            skSolve(sketch);
        }
        {
            var Q1;
            Q1 = qSketchRegion(id + "F317", true);
            var Q2;
            Q2 = qSketchRegion(id + "F320", true);
            loft(context, id + "F321", {"sheetProfilesArray" : [{ "sheetProfileEntities" : qUnion([Q1]) }, { "sheetProfileEntities" : qUnion([Q2]) }]});
        }
        {
            var Q0;
            Q0=qCreatedBy(id+"F316.planeOp",FACE);
            cPlane(context, id + "F322", {"entities" : qUnion([Q0]), "cplaneType" : CPlaneType.OFFSET, "offset" : 25 * mm, "width" : 150 * mm, "height" : 150 * mm});
        }
        {
            var Q0;
            Q0=qCreatedBy(id+"F322.planeOp",FACE);
            var sketch = newSketch(context, id + "F323", { "sketchPlane" : qUnion([Q0])});
            skLineSegment(sketch, "E432", {"start": v(-27.34, 91.3) * mm, "end": v(22.53, 94.9) * mm});
            skLineSegment(sketch, "E433", {"start": v(-27.34, -91.3) * mm, "end": v(22.53, -94.9) * mm});
            skArc(sketch, "E434", {"start": v(-27.34, -91.3) * mm, "mid": v(-24.04, 0) * mm, "end": v(-27.34, 91.3) * mm});
            skArc(sketch, "E435", {"start": v(22.53, -94.9) * mm, "mid": v(25.96, 0) * mm, "end": v(22.53, 94.9) * mm});
            skSolve(sketch);
        }
        {
            var Q1;
            Q1 = qSketchRegion(id + "F320", true);
            var Q2;
            Q2 = qSketchRegion(id + "F323", true);
            loft(context, id + "F324", {"sheetProfilesArray" : [{ "sheetProfileEntities" : qUnion([Q1]) }, { "sheetProfileEntities" : qUnion([Q2]) }]});
        }
        {
            var Q0;
            Q0=qCreatedBy(id+"F319.planeOp",FACE);
            cPlane(context, id + "F325", {"entities" : qUnion([Q0]), "cplaneType" : CPlaneType.OFFSET, "offset" : 25 * mm, "width" : 150 * mm, "height" : 150 * mm});
        }
        {
            var Q0;
            Q0=qCreatedBy(id+"F325.planeOp",FACE);
            var sketch = newSketch(context, id + "F326", { "sketchPlane" : qUnion([Q0])});
            skLineSegment(sketch, "E436", {"start": v(-27, 85.8) * mm, "end": v(22.88, 89.07) * mm});
            skLineSegment(sketch, "E437", {"start": v(-27, -85.8) * mm, "end": v(22.88, -89.07) * mm});
            skArc(sketch, "E438", {"start": v(-27, -85.8) * mm, "mid": v(-24.2, 0) * mm, "end": v(-27, 85.8) * mm});
            skArc(sketch, "E439", {"start": v(22.88, -89.07) * mm, "mid": v(25.8, 0) * mm, "end": v(22.88, 89.07) * mm});
            skSolve(sketch);
        }
        {
            var Q1;
            Q1 = qSketchRegion(id + "F323", true);
            var Q2;
            Q2 = qSketchRegion(id + "F326", true);
            loft(context, id + "F327", {"sheetProfilesArray" : [{ "sheetProfileEntities" : qUnion([Q1]) }, { "sheetProfileEntities" : qUnion([Q2]) }]});
        }
        {
            var Q0;
            Q0=qCreatedBy(id+"F322.planeOp",FACE);
            cPlane(context, id + "F328", {"entities" : qUnion([Q0]), "cplaneType" : CPlaneType.OFFSET, "offset" : 25 * mm, "width" : 150 * mm, "height" : 150 * mm});
        }
        {
            var Q0;
            Q0=qCreatedBy(id+"F328.planeOp",FACE);
            var sketch = newSketch(context, id + "F329", { "sketchPlane" : qUnion([Q0])});
            skLineSegment(sketch, "E440", {"start": v(-26.71, 80.3) * mm, "end": v(23.2, 83.24) * mm});
            skLineSegment(sketch, "E441", {"start": v(-26.71, -80.3) * mm, "end": v(23.2, -83.24) * mm});
            skArc(sketch, "E442", {"start": v(-26.71, -80.3) * mm, "mid": v(-24.35, 0) * mm, "end": v(-26.71, 80.3) * mm});
            skArc(sketch, "E443", {"start": v(23.2, -83.24) * mm, "mid": v(25.65, 0) * mm, "end": v(23.2, 83.24) * mm});
            skSolve(sketch);
        }
        {
            var Q1;
            Q1 = qSketchRegion(id + "F326", true);
            var Q2;
            Q2 = qSketchRegion(id + "F329", true);
            loft(context, id + "F330", {"sheetProfilesArray" : [{ "sheetProfileEntities" : qUnion([Q1]) }, { "sheetProfileEntities" : qUnion([Q2]) }]});
        }
        {
            var Q0;
            Q0=qCreatedBy(id+"F325.planeOp",FACE);
            cPlane(context, id + "F331", {"entities" : qUnion([Q0]), "cplaneType" : CPlaneType.OFFSET, "offset" : 25 * mm, "width" : 150 * mm, "height" : 150 * mm});
        }
        {
            var Q0;
            Q0=qCreatedBy(id+"F331.planeOp",FACE);
            var sketch = newSketch(context, id + "F332", { "sketchPlane" : qUnion([Q0])});
            skLineSegment(sketch, "E444", {"start": v(-26.45, 74.78) * mm, "end": v(23.48, 77.42) * mm});
            skLineSegment(sketch, "E445", {"start": v(-26.45, -74.78) * mm, "end": v(23.48, -77.42) * mm});
            skArc(sketch, "E446", {"start": v(-26.45, -74.78) * mm, "mid": v(-24.48, 0) * mm, "end": v(-26.45, 74.78) * mm});
            skArc(sketch, "E447", {"start": v(23.48, -77.42) * mm, "mid": v(25.52, 0) * mm, "end": v(23.48, 77.42) * mm});
            skSolve(sketch);
        }
        {
            var Q1;
            Q1 = qSketchRegion(id + "F329", true);
            var Q2;
            Q2 = qSketchRegion(id + "F332", true);
            loft(context, id + "F333", {"sheetProfilesArray" : [{ "sheetProfileEntities" : qUnion([Q1]) }, { "sheetProfileEntities" : qUnion([Q2]) }]});
        }
        {
            var Q0;
            Q0=qCreatedBy(id+"F328.planeOp",FACE);
            cPlane(context, id + "F334", {"entities" : qUnion([Q0]), "cplaneType" : CPlaneType.OFFSET, "offset" : 25 * mm, "width" : 150 * mm, "height" : 150 * mm});
        }
        {
            var Q0;
            Q0=qCreatedBy(id+"F334.planeOp",FACE);
            var sketch = newSketch(context, id + "F335", { "sketchPlane" : qUnion([Q0])});
            skLineSegment(sketch, "E448", {"start": v(-26.21, 69.25) * mm, "end": v(23.73, 71.6) * mm});
            skLineSegment(sketch, "E449", {"start": v(-26.21, -69.25) * mm, "end": v(23.73, -71.6) * mm});
            skArc(sketch, "E450", {"start": v(-26.21, -69.25) * mm, "mid": v(-24.59, 0) * mm, "end": v(-26.21, 69.25) * mm});
            skArc(sketch, "E451", {"start": v(23.73, -71.6) * mm, "mid": v(25.41, 0) * mm, "end": v(23.73, 71.6) * mm});
            skSolve(sketch);
        }
        {
            var Q1;
            Q1 = qSketchRegion(id + "F332", true);
            var Q2;
            Q2 = qSketchRegion(id + "F335", true);
            loft(context, id + "F336", {"sheetProfilesArray" : [{ "sheetProfileEntities" : qUnion([Q1]) }, { "sheetProfileEntities" : qUnion([Q2]) }]});
        }
        {
            var Q0;
            Q0=qCreatedBy(id+"F331.planeOp",FACE);
            cPlane(context, id + "F337", {"entities" : qUnion([Q0]), "cplaneType" : CPlaneType.OFFSET, "offset" : 25 * mm, "width" : 150 * mm, "height" : 150 * mm});
        }
        {
            var Q0;
            Q0=qCreatedBy(id+"F337.planeOp",FACE);
            var sketch = newSketch(context, id + "F338", { "sketchPlane" : qUnion([Q0])});
            skLineSegment(sketch, "E452", {"start": v(-26, 63.71) * mm, "end": v(23.95, 65.8) * mm});
            skLineSegment(sketch, "E453", {"start": v(-26, -63.71) * mm, "end": v(23.95, -65.8) * mm});
            skArc(sketch, "E454", {"start": v(-26, -63.71) * mm, "mid": v(-24.68, 0) * mm, "end": v(-26, 63.71) * mm});
            skArc(sketch, "E455", {"start": v(23.95, -65.8) * mm, "mid": v(25.32, 0) * mm, "end": v(23.95, 65.8) * mm});
            skSolve(sketch);
        }
        {
            var Q1;
            Q1 = qSketchRegion(id + "F335", true);
            var Q2;
            Q2 = qSketchRegion(id + "F338", true);
            loft(context, id + "F339", {"sheetProfilesArray" : [{ "sheetProfileEntities" : qUnion([Q1]) }, { "sheetProfileEntities" : qUnion([Q2]) }]});
        }
        {
            var Q0;
            Q0=qCreatedBy(id+"F334.planeOp",FACE);
            cPlane(context, id + "F340", {"entities" : qUnion([Q0]), "cplaneType" : CPlaneType.OFFSET, "offset" : 25 * mm, "width" : 150 * mm, "height" : 150 * mm});
        }
        {
            var Q0;
            Q0=qCreatedBy(id+"F340.planeOp",FACE);
            var sketch = newSketch(context, id + "F341", { "sketchPlane" : qUnion([Q0])});
            skLineSegment(sketch, "E456", {"start": v(-25.83, 58.16) * mm, "end": v(24.14, 60) * mm});
            skLineSegment(sketch, "E457", {"start": v(-25.83, -58.16) * mm, "end": v(24.14, -60) * mm});
            skArc(sketch, "E458", {"start": v(-25.83, -58.16) * mm, "mid": v(-24.77, 0) * mm, "end": v(-25.83, 58.16) * mm});
            skArc(sketch, "E459", {"start": v(24.14, -60) * mm, "mid": v(25.23, 0) * mm, "end": v(24.14, 60) * mm});
            skSolve(sketch);
        }
        {
            var Q1;
            Q1 = qSketchRegion(id + "F338", true);
            var Q2;
            Q2 = qSketchRegion(id + "F341", true);
            loft(context, id + "F342", {"sheetProfilesArray" : [{ "sheetProfileEntities" : qUnion([Q1]) }, { "sheetProfileEntities" : qUnion([Q2]) }]});
        }
        {
            var Q0;
            Q0=qCreatedBy(id+"F337.planeOp",FACE);
            cPlane(context, id + "F343", {"entities" : qUnion([Q0]), "cplaneType" : CPlaneType.OFFSET, "offset" : 25 * mm, "width" : 150 * mm, "height" : 150 * mm});
        }
        {
            var Q0;
            Q0=qCreatedBy(id+"F343.planeOp",FACE);
            var sketch = newSketch(context, id + "F344", { "sketchPlane" : qUnion([Q0])});
            skLineSegment(sketch, "E460", {"start": v(-25.68, 52.6) * mm, "end": v(24.3, 54.2) * mm});
            skLineSegment(sketch, "E461", {"start": v(-25.68, -52.6) * mm, "end": v(24.3, -54.2) * mm});
            skArc(sketch, "E462", {"start": v(-25.68, -52.6) * mm, "mid": v(-24.84, 0) * mm, "end": v(-25.68, 52.6) * mm});
            skArc(sketch, "E463", {"start": v(24.3, -54.2) * mm, "mid": v(25.16, 0) * mm, "end": v(24.3, 54.2) * mm});
            skSolve(sketch);
        }
        {
            var Q1;
            Q1 = qSketchRegion(id + "F341", true);
            var Q2;
            Q2 = qSketchRegion(id + "F344", true);
            loft(context, id + "F345", {"sheetProfilesArray" : [{ "sheetProfileEntities" : qUnion([Q1]) }, { "sheetProfileEntities" : qUnion([Q2]) }]});
        }
        {
            var Q0;
            Q0=qCreatedBy(id+"F340.planeOp",FACE);
            cPlane(context, id + "F346", {"entities" : qUnion([Q0]), "cplaneType" : CPlaneType.OFFSET, "offset" : 25 * mm, "width" : 150 * mm, "height" : 150 * mm});
        }
        {
            var Q0;
            Q0=qCreatedBy(id+"F346.planeOp",FACE);
            var sketch = newSketch(context, id + "F347", { "sketchPlane" : qUnion([Q0])});
            skLineSegment(sketch, "E464", {"start": v(-25.55, 47.04) * mm, "end": v(24.44, 48.4) * mm});
            skLineSegment(sketch, "E465", {"start": v(-25.55, -47.04) * mm, "end": v(24.44, -48.4) * mm});
            skArc(sketch, "E466", {"start": v(-25.55, -47.04) * mm, "mid": v(-24.9, 0) * mm, "end": v(-25.55, 47.04) * mm});
            skArc(sketch, "E467", {"start": v(24.44, -48.4) * mm, "mid": v(25.1, 0) * mm, "end": v(24.44, 48.4) * mm});
            skSolve(sketch);
        }
        {
            var Q1;
            Q1 = qSketchRegion(id + "F344", true);
            var Q2;
            Q2 = qSketchRegion(id + "F347", true);
            loft(context, id + "F348", {"sheetProfilesArray" : [{ "sheetProfileEntities" : qUnion([Q1]) }, { "sheetProfileEntities" : qUnion([Q2]) }]});
        }
        {
            var Q0;
            Q0=qCreatedBy(id+"F343.planeOp",FACE);
            cPlane(context, id + "F349", {"entities" : qUnion([Q0]), "cplaneType" : CPlaneType.OFFSET, "offset" : 25 * mm, "width" : 150 * mm, "height" : 150 * mm});
        }
        {
            var Q0;
            Q0=qCreatedBy(id+"F349.planeOp",FACE);
            var sketch = newSketch(context, id + "F350", { "sketchPlane" : qUnion([Q0])});
            skLineSegment(sketch, "E468", {"start": v(-25.43, 41.46) * mm, "end": v(24.55, 42.62) * mm});
            skLineSegment(sketch, "E469", {"start": v(-25.43, -41.46) * mm, "end": v(24.55, -42.62) * mm});
            skArc(sketch, "E470", {"start": v(-25.43, -41.46) * mm, "mid": v(-24.95, 0) * mm, "end": v(-25.43, 41.46) * mm});
            skArc(sketch, "E471", {"start": v(24.55, -42.62) * mm, "mid": v(25.05, 0) * mm, "end": v(24.55, 42.62) * mm});
            skSolve(sketch);
        }
        {
            var Q1;
            Q1 = qSketchRegion(id + "F347", true);
            var Q2;
            Q2 = qSketchRegion(id + "F350", true);
            loft(context, id + "F351", {"sheetProfilesArray" : [{ "sheetProfileEntities" : qUnion([Q1]) }, { "sheetProfileEntities" : qUnion([Q2]) }]});
        }
        {
            var Q0;
            Q0=qCreatedBy(id+"F346.planeOp",FACE);
            cPlane(context, id + "F352", {"entities" : qUnion([Q0]), "cplaneType" : CPlaneType.OFFSET, "offset" : 25 * mm, "width" : 150 * mm, "height" : 150 * mm});
        }
        {
            var Q0;
            Q0=qCreatedBy(id+"F352.planeOp",FACE);
            var sketch = newSketch(context, id + "F353", { "sketchPlane" : qUnion([Q0])});
            skLineSegment(sketch, "E472", {"start": v(-25.34, 35.88) * mm, "end": v(24.65, 36.84) * mm});
            skLineSegment(sketch, "E473", {"start": v(-25.34, -35.88) * mm, "end": v(24.65, -36.84) * mm});
            skArc(sketch, "E474", {"start": v(-25.34, -35.88) * mm, "mid": v(-25, 0) * mm, "end": v(-25.34, 35.88) * mm});
            skArc(sketch, "E475", {"start": v(24.65, -36.84) * mm, "mid": v(25, 0) * mm, "end": v(24.65, 36.84) * mm});
            skSolve(sketch);
        }
        {
            var Q1;
            Q1 = qSketchRegion(id + "F350", true);
            var Q2;
            Q2 = qSketchRegion(id + "F353", true);
            loft(context, id + "F354", {"sheetProfilesArray" : [{ "sheetProfileEntities" : qUnion([Q1]) }, { "sheetProfileEntities" : qUnion([Q2]) }]});
        }
        {
            var Q0;
            Q0=qCreatedBy(id+"F349.planeOp",FACE);
            cPlane(context, id + "F355", {"entities" : qUnion([Q0]), "cplaneType" : CPlaneType.OFFSET, "offset" : 25 * mm, "width" : 150 * mm, "height" : 150 * mm});
        }
        {
            var Q0;
            Q0=qCreatedBy(id+"F355.planeOp",FACE);
            var sketch = newSketch(context, id + "F356", { "sketchPlane" : qUnion([Q0])});
            skLineSegment(sketch, "E476", {"start": v(-25.26, 30.29) * mm, "end": v(24.73, 31.07) * mm});
            skLineSegment(sketch, "E477", {"start": v(-25.26, -30.29) * mm, "end": v(24.73, -31.07) * mm});
            skArc(sketch, "E478", {"start": v(-25.26, -30.29) * mm, "mid": v(-25.03, 0) * mm, "end": v(-25.26, 30.29) * mm});
            skArc(sketch, "E479", {"start": v(24.73, -31.07) * mm, "mid": v(24.97, 0) * mm, "end": v(24.73, 31.07) * mm});
            skSolve(sketch);
        }
        {
            var Q1;
            Q1 = qSketchRegion(id + "F353", true);
            var Q2;
            Q2 = qSketchRegion(id + "F356", true);
            loft(context, id + "F357", {"sheetProfilesArray" : [{ "sheetProfileEntities" : qUnion([Q1]) }, { "sheetProfileEntities" : qUnion([Q2]) }]});
        }
        {
            var Q0;
            Q0=qCreatedBy(id+"F352.planeOp",FACE);
            cPlane(context, id + "F358", {"entities" : qUnion([Q0]), "cplaneType" : CPlaneType.OFFSET, "offset" : 25 * mm, "width" : 150 * mm, "height" : 150 * mm});
        }
        {
            var Q0;
            Q0=qCreatedBy(id+"F358.planeOp",FACE);
            var sketch = newSketch(context, id + "F359", { "sketchPlane" : qUnion([Q0])});
            skLineSegment(sketch, "E480", {"start": v(-25.2, 24.7) * mm, "end": v(24.8, 25.3) * mm});
            skLineSegment(sketch, "E481", {"start": v(-25.2, -24.7) * mm, "end": v(24.8, -25.3) * mm});
            skArc(sketch, "E482", {"start": v(-25.2, -24.7) * mm, "mid": v(-25.05, 0) * mm, "end": v(-25.2, 24.7) * mm});
            skArc(sketch, "E483", {"start": v(24.8, -25.3) * mm, "mid": v(24.95, 0) * mm, "end": v(24.8, 25.3) * mm});
            skSolve(sketch);
        }
        {
            var Q1;
            Q1 = qSketchRegion(id + "F356", true);
            var Q2;
            Q2 = qSketchRegion(id + "F359", true);
            loft(context, id + "F360", {"sheetProfilesArray" : [{ "sheetProfileEntities" : qUnion([Q1]) }, { "sheetProfileEntities" : qUnion([Q2]) }]});
        }
    });
